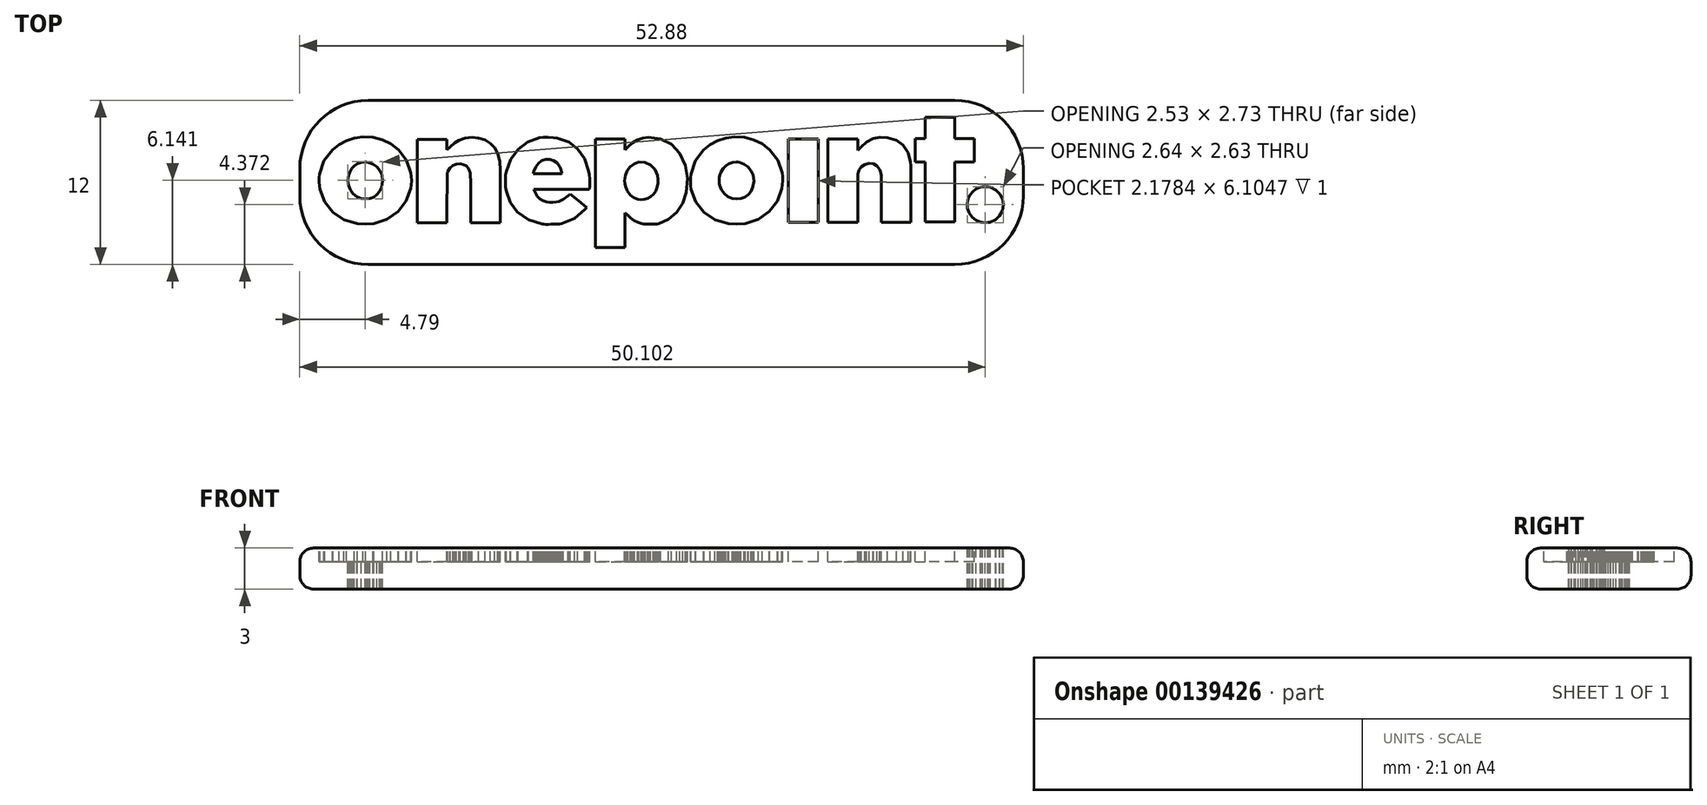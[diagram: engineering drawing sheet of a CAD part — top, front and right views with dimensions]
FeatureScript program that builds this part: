
annotation { "Feature Type Name" : "Feature", "Feature Type Description" : "" }
export const myFeature = defineFeature(function(context is Context, id is Id, definition is map)
    precondition{}
    {
        {
            var Q0;
            Q0=qCreatedBy(makeId("Top.planeOp"),FACE);
            var sketch = newSketch(context, id + "F0", { "sketchPlane" : qUnion([Q0])});
            skLineSegment(sketch, "E0", {"start": v(-22.22, -3.02) * mm, "end": v(-23.2, -2.73) * mm});
            skLineSegment(sketch, "E1", {"start": v(-23.2, -2.73) * mm, "end": v(-24, -2.19) * mm});
            skLineSegment(sketch, "E2", {"start": v(-24, -2.19) * mm, "end": v(-24.6, -1.44) * mm});
            skLineSegment(sketch, "E3", {"start": v(-24.6, -1.44) * mm, "end": v(-24.94, -0.52) * mm});
            skLineSegment(sketch, "E4", {"start": v(-24.94, -0.52) * mm, "end": v(-24.98, -0.27) * mm});
            skLineSegment(sketch, "E5", {"start": v(-24.98, -0.27) * mm, "end": v(-25, 0.03) * mm});
            skLineSegment(sketch, "E6", {"start": v(-25, 0.03) * mm, "end": v(-25, 0.33) * mm});
            skLineSegment(sketch, "E7", {"start": v(-25, 0.33) * mm, "end": v(-24.97, 0.6) * mm});
            skLineSegment(sketch, "E8", {"start": v(-24.97, 0.6) * mm, "end": v(-24.65, 1.57) * mm});
            skLineSegment(sketch, "E9", {"start": v(-24.65, 1.57) * mm, "end": v(-24.03, 2.4) * mm});
            skLineSegment(sketch, "E10", {"start": v(-24.03, 2.4) * mm, "end": v(-23.55, 2.77) * mm});
            skLineSegment(sketch, "E11", {"start": v(-23.55, 2.77) * mm, "end": v(-23.02, 3.06) * mm});
            skLineSegment(sketch, "E12", {"start": v(-23.02, 3.06) * mm, "end": v(-22.43, 3.24) * mm});
            skLineSegment(sketch, "E13", {"start": v(-22.43, 3.24) * mm, "end": v(-21.79, 3.32) * mm});
            skLineSegment(sketch, "E14", {"start": v(-21.79, 3.32) * mm, "end": v(-21.06, 3.29) * mm});
            skLineSegment(sketch, "E15", {"start": v(-21.06, 3.29) * mm, "end": v(-20.38, 3.12) * mm});
            skLineSegment(sketch, "E16", {"start": v(-20.38, 3.12) * mm, "end": v(-19.76, 2.82) * mm});
            skLineSegment(sketch, "E17", {"start": v(-19.76, 2.82) * mm, "end": v(-19.21, 2.4) * mm});
            skLineSegment(sketch, "E18", {"start": v(-19.21, 2.4) * mm, "end": v(-18.61, 1.6) * mm});
            skLineSegment(sketch, "E19", {"start": v(-18.61, 1.6) * mm, "end": v(-18.3, 0.69) * mm});
            skLineSegment(sketch, "E20", {"start": v(-18.3, 0.69) * mm, "end": v(-18.26, 0.43) * mm});
            skLineSegment(sketch, "E21", {"start": v(-18.26, 0.43) * mm, "end": v(-18.26, 0.12) * mm});
            skLineSegment(sketch, "E22", {"start": v(-18.26, 0.12) * mm, "end": v(-18.27, -0.18) * mm});
            skLineSegment(sketch, "E23", {"start": v(-18.27, -0.18) * mm, "end": v(-18.3, -0.44) * mm});
            skLineSegment(sketch, "E24", {"start": v(-18.3, -0.44) * mm, "end": v(-18.64, -1.38) * mm});
            skLineSegment(sketch, "E25", {"start": v(-18.64, -1.38) * mm, "end": v(-19.24, -2.14) * mm});
            skLineSegment(sketch, "E26", {"start": v(-19.24, -2.14) * mm, "end": v(-20.04, -2.7) * mm});
            skLineSegment(sketch, "E27", {"start": v(-20.04, -2.7) * mm, "end": v(-21, -3) * mm});
            skLineSegment(sketch, "E28", {"start": v(-21, -3) * mm, "end": v(-21.62, -3.05) * mm});
            skLineSegment(sketch, "E29", {"start": v(-21.62, -3.05) * mm, "end": v(-22.22, -3.02) * mm});
            skLineSegment(sketch, "E30", {"start": v(-22.22, -3.02) * mm, "end": v(-22.22, -3.02) * mm});
            skLineSegment(sketch, "E31", {"start": v(-21.3, -1.19) * mm, "end": v(-21.02, -1.07) * mm});
            skLineSegment(sketch, "E32", {"start": v(-21.02, -1.07) * mm, "end": v(-20.78, -0.9) * mm});
            skLineSegment(sketch, "E33", {"start": v(-20.78, -0.9) * mm, "end": v(-20.59, -0.66) * mm});
            skLineSegment(sketch, "E34", {"start": v(-20.59, -0.66) * mm, "end": v(-20.44, -0.36) * mm});
            skLineSegment(sketch, "E35", {"start": v(-20.44, -0.36) * mm, "end": v(-20.36, 0.1) * mm});
            skLineSegment(sketch, "E36", {"start": v(-20.36, 0.1) * mm, "end": v(-20.41, 0.53) * mm});
            skLineSegment(sketch, "E37", {"start": v(-20.41, 0.53) * mm, "end": v(-20.57, 0.87) * mm});
            skLineSegment(sketch, "E38", {"start": v(-20.57, 0.87) * mm, "end": v(-20.8, 1.14) * mm});
            skLineSegment(sketch, "E39", {"start": v(-20.8, 1.14) * mm, "end": v(-21.07, 1.34) * mm});
            skLineSegment(sketch, "E40", {"start": v(-21.07, 1.34) * mm, "end": v(-21.4, 1.46) * mm});
            skLineSegment(sketch, "E41", {"start": v(-21.4, 1.46) * mm, "end": v(-21.54, 1.5) * mm});
            skLineSegment(sketch, "E42", {"start": v(-21.54, 1.5) * mm, "end": v(-21.65, 1.5) * mm});
            skLineSegment(sketch, "E43", {"start": v(-21.65, 1.5) * mm, "end": v(-21.92, 1.46) * mm});
            skLineSegment(sketch, "E44", {"start": v(-21.92, 1.46) * mm, "end": v(-22.2, 1.36) * mm});
            skLineSegment(sketch, "E45", {"start": v(-22.2, 1.36) * mm, "end": v(-22.42, 1.21) * mm});
            skLineSegment(sketch, "E46", {"start": v(-22.42, 1.21) * mm, "end": v(-22.61, 1) * mm});
            skLineSegment(sketch, "E47", {"start": v(-22.61, 1) * mm, "end": v(-22.76, 0.77) * mm});
            skLineSegment(sketch, "E48", {"start": v(-22.76, 0.77) * mm, "end": v(-22.85, 0.52) * mm});
            skLineSegment(sketch, "E49", {"start": v(-22.85, 0.52) * mm, "end": v(-22.88, 0.34) * mm});
            skLineSegment(sketch, "E50", {"start": v(-22.88, 0.34) * mm, "end": v(-22.9, 0.14) * mm});
            skLineSegment(sketch, "E51", {"start": v(-22.9, 0.14) * mm, "end": v(-22.88, -0.06) * mm});
            skLineSegment(sketch, "E52", {"start": v(-22.88, -0.06) * mm, "end": v(-22.85, -0.21) * mm});
            skLineSegment(sketch, "E53", {"start": v(-22.85, -0.21) * mm, "end": v(-22.72, -0.55) * mm});
            skLineSegment(sketch, "E54", {"start": v(-22.72, -0.55) * mm, "end": v(-22.52, -0.84) * mm});
            skLineSegment(sketch, "E55", {"start": v(-22.52, -0.84) * mm, "end": v(-22.25, -1.06) * mm});
            skLineSegment(sketch, "E56", {"start": v(-22.25, -1.06) * mm, "end": v(-21.93, -1.19) * mm});
            skLineSegment(sketch, "E57", {"start": v(-21.93, -1.19) * mm, "end": v(-21.62, -1.22) * mm});
            skLineSegment(sketch, "E58", {"start": v(-21.62, -1.22) * mm, "end": v(-21.3, -1.19) * mm});
            skLineSegment(sketch, "E59", {"start": v(-21.3, -1.19) * mm, "end": v(-21.3, -1.19) * mm});
            skLineSegment(sketch, "E60", {"start": v(-17.82, 0.1) * mm, "end": v(-17.82, 3.15) * mm});
            skLineSegment(sketch, "E61", {"start": v(-17.82, 3.15) * mm, "end": v(-15.66, 3.15) * mm});
            skLineSegment(sketch, "E62", {"start": v(-15.66, 3.15) * mm, "end": v(-15.66, 2.36) * mm});
            skLineSegment(sketch, "E63", {"start": v(-15.66, 2.36) * mm, "end": v(-15.43, 2.6) * mm});
            skLineSegment(sketch, "E64", {"start": v(-15.43, 2.6) * mm, "end": v(-15.1, 2.89) * mm});
            skLineSegment(sketch, "E65", {"start": v(-15.1, 2.89) * mm, "end": v(-14.77, 3.08) * mm});
            skLineSegment(sketch, "E66", {"start": v(-14.77, 3.08) * mm, "end": v(-14.32, 3.24) * mm});
            skLineSegment(sketch, "E67", {"start": v(-14.32, 3.24) * mm, "end": v(-13.83, 3.3) * mm});
            skLineSegment(sketch, "E68", {"start": v(-13.83, 3.3) * mm, "end": v(-13.34, 3.25) * mm});
            skLineSegment(sketch, "E69", {"start": v(-13.34, 3.25) * mm, "end": v(-12.88, 3.1) * mm});
            skLineSegment(sketch, "E70", {"start": v(-12.88, 3.1) * mm, "end": v(-12.5, 2.86) * mm});
            skLineSegment(sketch, "E71", {"start": v(-12.5, 2.86) * mm, "end": v(-12.2, 2.54) * mm});
            skLineSegment(sketch, "E72", {"start": v(-12.2, 2.54) * mm, "end": v(-11.97, 2.13) * mm});
            skLineSegment(sketch, "E73", {"start": v(-11.97, 2.13) * mm, "end": v(-11.82, 1.63) * mm});
            skLineSegment(sketch, "E74", {"start": v(-11.82, 1.63) * mm, "end": v(-11.8, 1.57) * mm});
            skLineSegment(sketch, "E75", {"start": v(-11.8, 1.57) * mm, "end": v(-11.8, 1.47) * mm});
            skLineSegment(sketch, "E76", {"start": v(-11.8, 1.47) * mm, "end": v(-11.78, 1.32) * mm});
            skLineSegment(sketch, "E77", {"start": v(-11.78, 1.32) * mm, "end": v(-11.78, 1.11) * mm});
            skLineSegment(sketch, "E78", {"start": v(-11.78, 1.11) * mm, "end": v(-11.77, 0.82) * mm});
            skLineSegment(sketch, "E79", {"start": v(-11.77, 0.82) * mm, "end": v(-11.77, 0.42) * mm});
            skLineSegment(sketch, "E80", {"start": v(-11.77, 0.42) * mm, "end": v(-11.76, -0.1) * mm});
            skLineSegment(sketch, "E81", {"start": v(-11.76, -0.1) * mm, "end": v(-11.76, -0.75) * mm});
            skLineSegment(sketch, "E82", {"start": v(-11.76, -0.75) * mm, "end": v(-11.76, -2.95) * mm});
            skLineSegment(sketch, "E83", {"start": v(-11.76, -2.95) * mm, "end": v(-13.92, -2.95) * mm});
            skLineSegment(sketch, "E84", {"start": v(-13.92, -2.95) * mm, "end": v(-13.92, -1.18) * mm});
            skLineSegment(sketch, "E85", {"start": v(-13.92, -1.18) * mm, "end": v(-13.93, -0.6) * mm});
            skLineSegment(sketch, "E86", {"start": v(-13.93, -0.6) * mm, "end": v(-13.93, -0.15) * mm});
            skLineSegment(sketch, "E87", {"start": v(-13.93, -0.15) * mm, "end": v(-13.94, 0.17) * mm});
            skLineSegment(sketch, "E88", {"start": v(-13.94, 0.17) * mm, "end": v(-13.94, 0.4) * mm});
            skLineSegment(sketch, "E89", {"start": v(-13.94, 0.4) * mm, "end": v(-13.95, 0.55) * mm});
            skLineSegment(sketch, "E90", {"start": v(-13.95, 0.55) * mm, "end": v(-13.96, 0.64) * mm});
            skLineSegment(sketch, "E91", {"start": v(-13.96, 0.64) * mm, "end": v(-13.97, 0.7) * mm});
            skLineSegment(sketch, "E92", {"start": v(-13.97, 0.7) * mm, "end": v(-13.98, 0.76) * mm});
            skLineSegment(sketch, "E93", {"start": v(-13.98, 0.76) * mm, "end": v(-14.1, 1) * mm});
            skLineSegment(sketch, "E94", {"start": v(-14.1, 1) * mm, "end": v(-14.25, 1.19) * mm});
            skLineSegment(sketch, "E95", {"start": v(-14.25, 1.19) * mm, "end": v(-14.45, 1.3) * mm});
            skLineSegment(sketch, "E96", {"start": v(-14.45, 1.3) * mm, "end": v(-14.7, 1.36) * mm});
            skLineSegment(sketch, "E97", {"start": v(-14.7, 1.36) * mm, "end": v(-14.99, 1.34) * mm});
            skLineSegment(sketch, "E98", {"start": v(-14.99, 1.34) * mm, "end": v(-15.24, 1.24) * mm});
            skLineSegment(sketch, "E99", {"start": v(-15.24, 1.24) * mm, "end": v(-15.45, 1.05) * mm});
            skLineSegment(sketch, "E100", {"start": v(-15.45, 1.05) * mm, "end": v(-15.6, 0.79) * mm});
            skLineSegment(sketch, "E101", {"start": v(-15.6, 0.79) * mm, "end": v(-15.62, 0.74) * mm});
            skLineSegment(sketch, "E102", {"start": v(-15.62, 0.74) * mm, "end": v(-15.63, 0.68) * mm});
            skLineSegment(sketch, "E103", {"start": v(-15.63, 0.68) * mm, "end": v(-15.63, 0.59) * mm});
            skLineSegment(sketch, "E104", {"start": v(-15.63, 0.59) * mm, "end": v(-15.64, 0.44) * mm});
            skLineSegment(sketch, "E105", {"start": v(-15.64, 0.44) * mm, "end": v(-15.65, 0.21) * mm});
            skLineSegment(sketch, "E106", {"start": v(-15.65, 0.21) * mm, "end": v(-15.65, -0.11) * mm});
            skLineSegment(sketch, "E107", {"start": v(-15.65, -0.11) * mm, "end": v(-15.65, -0.56) * mm});
            skLineSegment(sketch, "E108", {"start": v(-15.65, -0.56) * mm, "end": v(-15.66, -1.15) * mm});
            skLineSegment(sketch, "E109", {"start": v(-15.66, -1.15) * mm, "end": v(-15.66, -2.95) * mm});
            skLineSegment(sketch, "E110", {"start": v(-15.66, -2.95) * mm, "end": v(-17.82, -2.95) * mm});
            skLineSegment(sketch, "E111", {"start": v(-17.82, -2.95) * mm, "end": v(-17.82, 0.1) * mm});
            skLineSegment(sketch, "E112", {"start": v(-17.82, 0.1) * mm, "end": v(-17.82, 0.1) * mm});
            skLineSegment(sketch, "E113", {"start": v(-8.68, -3.05) * mm, "end": v(-9.7, -2.75) * mm});
            skLineSegment(sketch, "E114", {"start": v(-9.7, -2.75) * mm, "end": v(-10.51, -2.16) * mm});
            skLineSegment(sketch, "E115", {"start": v(-10.51, -2.16) * mm, "end": v(-11.03, -1.47) * mm});
            skLineSegment(sketch, "E116", {"start": v(-11.03, -1.47) * mm, "end": v(-11.33, -0.63) * mm});
            skLineSegment(sketch, "E117", {"start": v(-11.33, -0.63) * mm, "end": v(-11.36, -0.5) * mm});
            skLineSegment(sketch, "E118", {"start": v(-11.36, -0.5) * mm, "end": v(-11.37, -0.35) * mm});
            skLineSegment(sketch, "E119", {"start": v(-11.37, -0.35) * mm, "end": v(-11.38, -0.17) * mm});
            skLineSegment(sketch, "E120", {"start": v(-11.38, -0.17) * mm, "end": v(-11.39, 0.09) * mm});
            skLineSegment(sketch, "E121", {"start": v(-11.39, 0.09) * mm, "end": v(-11.38, 0.35) * mm});
            skLineSegment(sketch, "E122", {"start": v(-11.38, 0.35) * mm, "end": v(-11.37, 0.53) * mm});
            skLineSegment(sketch, "E123", {"start": v(-11.37, 0.53) * mm, "end": v(-11.36, 0.66) * mm});
            skLineSegment(sketch, "E124", {"start": v(-11.36, 0.66) * mm, "end": v(-11.33, 0.8) * mm});
            skLineSegment(sketch, "E125", {"start": v(-11.33, 0.8) * mm, "end": v(-11.01, 1.7) * mm});
            skLineSegment(sketch, "E126", {"start": v(-11.01, 1.7) * mm, "end": v(-10.47, 2.42) * mm});
            skLineSegment(sketch, "E127", {"start": v(-10.47, 2.42) * mm, "end": v(-9.76, 2.96) * mm});
            skLineSegment(sketch, "E128", {"start": v(-9.76, 2.96) * mm, "end": v(-8.9, 3.25) * mm});
            skLineSegment(sketch, "E129", {"start": v(-8.9, 3.25) * mm, "end": v(-8.62, 3.29) * mm});
            skLineSegment(sketch, "E130", {"start": v(-8.62, 3.29) * mm, "end": v(-8.26, 3.3) * mm});
            skLineSegment(sketch, "E131", {"start": v(-8.26, 3.3) * mm, "end": v(-7.9, 3.28) * mm});
            skLineSegment(sketch, "E132", {"start": v(-7.9, 3.28) * mm, "end": v(-7.6, 3.24) * mm});
            skLineSegment(sketch, "E133", {"start": v(-7.6, 3.24) * mm, "end": v(-6.76, 2.95) * mm});
            skLineSegment(sketch, "E134", {"start": v(-6.76, 2.95) * mm, "end": v(-6.1, 2.44) * mm});
            skLineSegment(sketch, "E135", {"start": v(-6.1, 2.44) * mm, "end": v(-5.61, 1.73) * mm});
            skLineSegment(sketch, "E136", {"start": v(-5.61, 1.73) * mm, "end": v(-5.3, 0.85) * mm});
            skLineSegment(sketch, "E137", {"start": v(-5.3, 0.85) * mm, "end": v(-5.27, 0.57) * mm});
            skLineSegment(sketch, "E138", {"start": v(-5.27, 0.57) * mm, "end": v(-5.24, 0.24) * mm});
            skLineSegment(sketch, "E139", {"start": v(-5.24, 0.24) * mm, "end": v(-5.22, -0.08) * mm});
            skLineSegment(sketch, "E140", {"start": v(-5.22, -0.08) * mm, "end": v(-5.22, -0.32) * mm});
            skLineSegment(sketch, "E141", {"start": v(-5.22, -0.32) * mm, "end": v(-5.25, -0.5) * mm});
            skLineSegment(sketch, "E142", {"start": v(-5.25, -0.5) * mm, "end": v(-9.3, -0.5) * mm});
            skLineSegment(sketch, "E143", {"start": v(-9.3, -0.5) * mm, "end": v(-9.3, -0.56) * mm});
            skLineSegment(sketch, "E144", {"start": v(-9.3, -0.56) * mm, "end": v(-9.27, -0.64) * mm});
            skLineSegment(sketch, "E145", {"start": v(-9.27, -0.64) * mm, "end": v(-9.2, -0.77) * mm});
            skLineSegment(sketch, "E146", {"start": v(-9.2, -0.77) * mm, "end": v(-9.06, -1) * mm});
            skLineSegment(sketch, "E147", {"start": v(-9.06, -1) * mm, "end": v(-8.87, -1.2) * mm});
            skLineSegment(sketch, "E148", {"start": v(-8.87, -1.2) * mm, "end": v(-8.64, -1.34) * mm});
            skLineSegment(sketch, "E149", {"start": v(-8.64, -1.34) * mm, "end": v(-8.38, -1.43) * mm});
            skLineSegment(sketch, "E150", {"start": v(-8.38, -1.43) * mm, "end": v(-8.16, -1.46) * mm});
            skLineSegment(sketch, "E151", {"start": v(-8.16, -1.46) * mm, "end": v(-7.92, -1.46) * mm});
            skLineSegment(sketch, "E152", {"start": v(-7.92, -1.46) * mm, "end": v(-7.68, -1.44) * mm});
            skLineSegment(sketch, "E153", {"start": v(-7.68, -1.44) * mm, "end": v(-7.47, -1.4) * mm});
            skLineSegment(sketch, "E154", {"start": v(-7.47, -1.4) * mm, "end": v(-7.15, -1.23) * mm});
            skLineSegment(sketch, "E155", {"start": v(-7.15, -1.23) * mm, "end": v(-6.83, -0.99) * mm});
            skLineSegment(sketch, "E156", {"start": v(-6.83, -0.99) * mm, "end": v(-6.66, -0.85) * mm});
            skLineSegment(sketch, "E157", {"start": v(-6.66, -0.85) * mm, "end": v(-6.05, -1.35) * mm});
            skLineSegment(sketch, "E158", {"start": v(-6.05, -1.35) * mm, "end": v(-5.45, -1.85) * mm});
            skLineSegment(sketch, "E159", {"start": v(-5.45, -1.85) * mm, "end": v(-5.57, -1.98) * mm});
            skLineSegment(sketch, "E160", {"start": v(-5.57, -1.98) * mm, "end": v(-6.33, -2.63) * mm});
            skLineSegment(sketch, "E161", {"start": v(-6.33, -2.63) * mm, "end": v(-7.29, -3) * mm});
            skLineSegment(sketch, "E162", {"start": v(-7.29, -3) * mm, "end": v(-7.43, -3.04) * mm});
            skLineSegment(sketch, "E163", {"start": v(-7.43, -3.04) * mm, "end": v(-7.58, -3.05) * mm});
            skLineSegment(sketch, "E164", {"start": v(-7.58, -3.05) * mm, "end": v(-7.77, -3.06) * mm});
            skLineSegment(sketch, "E165", {"start": v(-7.77, -3.06) * mm, "end": v(-8.05, -3.07) * mm});
            skLineSegment(sketch, "E166", {"start": v(-8.05, -3.07) * mm, "end": v(-8.25, -3.07) * mm});
            skLineSegment(sketch, "E167", {"start": v(-8.25, -3.07) * mm, "end": v(-8.44, -3.07) * mm});
            skLineSegment(sketch, "E168", {"start": v(-8.44, -3.07) * mm, "end": v(-8.59, -3.06) * mm});
            skLineSegment(sketch, "E169", {"start": v(-8.59, -3.06) * mm, "end": v(-8.68, -3.05) * mm});
            skLineSegment(sketch, "E170", {"start": v(-8.68, -3.05) * mm, "end": v(-8.68, -3.05) * mm});
            skLineSegment(sketch, "E171", {"start": v(-7.26, 0.66) * mm, "end": v(-7.27, 0.75) * mm});
            skLineSegment(sketch, "E172", {"start": v(-7.27, 0.75) * mm, "end": v(-7.31, 0.88) * mm});
            skLineSegment(sketch, "E173", {"start": v(-7.31, 0.88) * mm, "end": v(-7.36, 1.02) * mm});
            skLineSegment(sketch, "E174", {"start": v(-7.36, 1.02) * mm, "end": v(-7.42, 1.15) * mm});
            skLineSegment(sketch, "E175", {"start": v(-7.42, 1.15) * mm, "end": v(-7.6, 1.41) * mm});
            skLineSegment(sketch, "E176", {"start": v(-7.6, 1.41) * mm, "end": v(-7.85, 1.6) * mm});
            skLineSegment(sketch, "E177", {"start": v(-7.85, 1.6) * mm, "end": v(-8.14, 1.7) * mm});
            skLineSegment(sketch, "E178", {"start": v(-8.14, 1.7) * mm, "end": v(-8.46, 1.7) * mm});
            skLineSegment(sketch, "E179", {"start": v(-8.46, 1.7) * mm, "end": v(-8.75, 1.59) * mm});
            skLineSegment(sketch, "E180", {"start": v(-8.75, 1.59) * mm, "end": v(-8.99, 1.4) * mm});
            skLineSegment(sketch, "E181", {"start": v(-8.99, 1.4) * mm, "end": v(-9.17, 1.14) * mm});
            skLineSegment(sketch, "E182", {"start": v(-9.17, 1.14) * mm, "end": v(-9.3, 0.8) * mm});
            skLineSegment(sketch, "E183", {"start": v(-9.3, 0.8) * mm, "end": v(-9.35, 0.63) * mm});
            skLineSegment(sketch, "E184", {"start": v(-9.35, 0.63) * mm, "end": v(-8.3, 0.63) * mm});
            skLineSegment(sketch, "E185", {"start": v(-8.3, 0.63) * mm, "end": v(-7.99, 0.63) * mm});
            skLineSegment(sketch, "E186", {"start": v(-7.99, 0.63) * mm, "end": v(-7.74, 0.63) * mm});
            skLineSegment(sketch, "E187", {"start": v(-7.74, 0.63) * mm, "end": v(-7.56, 0.63) * mm});
            skLineSegment(sketch, "E188", {"start": v(-7.56, 0.63) * mm, "end": v(-7.43, 0.63) * mm});
            skLineSegment(sketch, "E189", {"start": v(-7.43, 0.63) * mm, "end": v(-7.34, 0.64) * mm});
            skLineSegment(sketch, "E190", {"start": v(-7.34, 0.64) * mm, "end": v(-7.29, 0.64) * mm});
            skLineSegment(sketch, "E191", {"start": v(-7.29, 0.64) * mm, "end": v(-7.27, 0.65) * mm});
            skLineSegment(sketch, "E192", {"start": v(-7.27, 0.65) * mm, "end": v(-7.26, 0.66) * mm});
            skLineSegment(sketch, "E193", {"start": v(-7.26, 0.66) * mm, "end": v(-7.26, 0.66) * mm});
            skLineSegment(sketch, "E194", {"start": v(-4.8, -0.79) * mm, "end": v(-4.8, 3.17) * mm});
            skLineSegment(sketch, "E195", {"start": v(-4.8, 3.17) * mm, "end": v(-2.64, 3.17) * mm});
            skLineSegment(sketch, "E196", {"start": v(-2.64, 3.17) * mm, "end": v(-2.64, 2.38) * mm});
            skLineSegment(sketch, "E197", {"start": v(-2.64, 2.38) * mm, "end": v(-2.44, 2.6) * mm});
            skLineSegment(sketch, "E198", {"start": v(-2.44, 2.6) * mm, "end": v(-2.1, 2.9) * mm});
            skLineSegment(sketch, "E199", {"start": v(-2.1, 2.9) * mm, "end": v(-1.74, 3.1) * mm});
            skLineSegment(sketch, "E200", {"start": v(-1.74, 3.1) * mm, "end": v(-1.36, 3.24) * mm});
            skLineSegment(sketch, "E201", {"start": v(-1.36, 3.24) * mm, "end": v(-0.92, 3.3) * mm});
            skLineSegment(sketch, "E202", {"start": v(-0.92, 3.3) * mm, "end": v(-0.04, 3.18) * mm});
            skLineSegment(sketch, "E203", {"start": v(-0.04, 3.18) * mm, "end": v(0.74, 2.78) * mm});
            skLineSegment(sketch, "E204", {"start": v(0.74, 2.78) * mm, "end": v(1.35, 2.12) * mm});
            skLineSegment(sketch, "E205", {"start": v(1.35, 2.12) * mm, "end": v(1.76, 1.25) * mm});
            skLineSegment(sketch, "E206", {"start": v(1.76, 1.25) * mm, "end": v(1.9, 0.27) * mm});
            skLineSegment(sketch, "E207", {"start": v(1.9, 0.27) * mm, "end": v(1.83, -0.73) * mm});
            skLineSegment(sketch, "E208", {"start": v(1.83, -0.73) * mm, "end": v(1.56, -1.53) * mm});
            skLineSegment(sketch, "E209", {"start": v(1.56, -1.53) * mm, "end": v(1.12, -2.2) * mm});
            skLineSegment(sketch, "E210", {"start": v(1.12, -2.2) * mm, "end": v(0.54, -2.7) * mm});
            skLineSegment(sketch, "E211", {"start": v(0.54, -2.7) * mm, "end": v(-0.17, -3) * mm});
            skLineSegment(sketch, "E212", {"start": v(-0.17, -3) * mm, "end": v(-0.3, -3.04) * mm});
            skLineSegment(sketch, "E213", {"start": v(-0.3, -3.04) * mm, "end": v(-0.43, -3.06) * mm});
            skLineSegment(sketch, "E214", {"start": v(-0.43, -3.06) * mm, "end": v(-0.58, -3.07) * mm});
            skLineSegment(sketch, "E215", {"start": v(-0.58, -3.07) * mm, "end": v(-0.8, -3.07) * mm});
            skLineSegment(sketch, "E216", {"start": v(-0.8, -3.07) * mm, "end": v(-1.02, -3.07) * mm});
            skLineSegment(sketch, "E217", {"start": v(-1.02, -3.07) * mm, "end": v(-1.17, -3.06) * mm});
            skLineSegment(sketch, "E218", {"start": v(-1.17, -3.06) * mm, "end": v(-1.3, -3.04) * mm});
            skLineSegment(sketch, "E219", {"start": v(-1.3, -3.04) * mm, "end": v(-1.43, -3) * mm});
            skLineSegment(sketch, "E220", {"start": v(-1.43, -3) * mm, "end": v(-1.71, -2.91) * mm});
            skLineSegment(sketch, "E221", {"start": v(-1.71, -2.91) * mm, "end": v(-1.98, -2.78) * mm});
            skLineSegment(sketch, "E222", {"start": v(-1.98, -2.78) * mm, "end": v(-2.23, -2.61) * mm});
            skLineSegment(sketch, "E223", {"start": v(-2.23, -2.61) * mm, "end": v(-2.47, -2.4) * mm});
            skLineSegment(sketch, "E224", {"start": v(-2.47, -2.4) * mm, "end": v(-2.64, -2.24) * mm});
            skLineSegment(sketch, "E225", {"start": v(-2.64, -2.24) * mm, "end": v(-2.64, -4.76) * mm});
            skLineSegment(sketch, "E226", {"start": v(-2.64, -4.76) * mm, "end": v(-4.8, -4.76) * mm});
            skLineSegment(sketch, "E227", {"start": v(-4.8, -4.76) * mm, "end": v(-4.8, -0.79) * mm});
            skLineSegment(sketch, "E228", {"start": v(-4.8, -0.79) * mm, "end": v(-4.8, -0.79) * mm});
            skLineSegment(sketch, "E229", {"start": v(-1.25, -1.25) * mm, "end": v(-1, -1.18) * mm});
            skLineSegment(sketch, "E230", {"start": v(-1, -1.18) * mm, "end": v(-0.77, -1.04) * mm});
            skLineSegment(sketch, "E231", {"start": v(-0.77, -1.04) * mm, "end": v(-0.56, -0.85) * mm});
            skLineSegment(sketch, "E232", {"start": v(-0.56, -0.85) * mm, "end": v(-0.4, -0.63) * mm});
            skLineSegment(sketch, "E233", {"start": v(-0.4, -0.63) * mm, "end": v(-0.3, -0.36) * mm});
            skLineSegment(sketch, "E234", {"start": v(-0.3, -0.36) * mm, "end": v(-0.24, -0.07) * mm});
            skLineSegment(sketch, "E235", {"start": v(-0.24, -0.07) * mm, "end": v(-0.23, 0.23) * mm});
            skLineSegment(sketch, "E236", {"start": v(-0.23, 0.23) * mm, "end": v(-0.28, 0.52) * mm});
            skLineSegment(sketch, "E237", {"start": v(-0.28, 0.52) * mm, "end": v(-0.47, 0.95) * mm});
            skLineSegment(sketch, "E238", {"start": v(-0.47, 0.95) * mm, "end": v(-0.78, 1.27) * mm});
            skLineSegment(sketch, "E239", {"start": v(-0.78, 1.27) * mm, "end": v(-1.18, 1.45) * mm});
            skLineSegment(sketch, "E240", {"start": v(-1.18, 1.45) * mm, "end": v(-1.63, 1.48) * mm});
            skLineSegment(sketch, "E241", {"start": v(-1.63, 1.48) * mm, "end": v(-1.97, 1.37) * mm});
            skLineSegment(sketch, "E242", {"start": v(-1.97, 1.37) * mm, "end": v(-2.26, 1.16) * mm});
            skLineSegment(sketch, "E243", {"start": v(-2.26, 1.16) * mm, "end": v(-2.49, 0.86) * mm});
            skLineSegment(sketch, "E244", {"start": v(-2.49, 0.86) * mm, "end": v(-2.63, 0.5) * mm});
            skLineSegment(sketch, "E245", {"start": v(-2.63, 0.5) * mm, "end": v(-2.66, 0.33) * mm});
            skLineSegment(sketch, "E246", {"start": v(-2.66, 0.33) * mm, "end": v(-2.67, 0.11) * mm});
            skLineSegment(sketch, "E247", {"start": v(-2.67, 0.11) * mm, "end": v(-2.66, -0.1) * mm});
            skLineSegment(sketch, "E248", {"start": v(-2.66, -0.1) * mm, "end": v(-2.63, -0.27) * mm});
            skLineSegment(sketch, "E249", {"start": v(-2.63, -0.27) * mm, "end": v(-2.5, -0.62) * mm});
            skLineSegment(sketch, "E250", {"start": v(-2.5, -0.62) * mm, "end": v(-2.29, -0.9) * mm});
            skLineSegment(sketch, "E251", {"start": v(-2.29, -0.9) * mm, "end": v(-2.02, -1.12) * mm});
            skLineSegment(sketch, "E252", {"start": v(-2.02, -1.12) * mm, "end": v(-1.7, -1.25) * mm});
            skLineSegment(sketch, "E253", {"start": v(-1.7, -1.25) * mm, "end": v(-1.48, -1.27) * mm});
            skLineSegment(sketch, "E254", {"start": v(-1.48, -1.27) * mm, "end": v(-1.25, -1.25) * mm});
            skLineSegment(sketch, "E255", {"start": v(9.3, 0.11) * mm, "end": v(9.3, 3.17) * mm});
            skLineSegment(sketch, "E256", {"start": v(9.3, 3.17) * mm, "end": v(11.47, 3.17) * mm});
            skLineSegment(sketch, "E257", {"start": v(11.47, 3.17) * mm, "end": v(11.47, -2.94) * mm});
            skLineSegment(sketch, "E258", {"start": v(11.47, -2.94) * mm, "end": v(9.3, -2.94) * mm});
            skLineSegment(sketch, "E259", {"start": v(9.3, -2.94) * mm, "end": v(9.3, 0.11) * mm});
            skLineSegment(sketch, "E260", {"start": v(4.9, -3.02) * mm, "end": v(3.94, -2.73) * mm});
            skLineSegment(sketch, "E261", {"start": v(3.94, -2.73) * mm, "end": v(3.13, -2.19) * mm});
            skLineSegment(sketch, "E262", {"start": v(3.13, -2.19) * mm, "end": v(2.54, -1.44) * mm});
            skLineSegment(sketch, "E263", {"start": v(2.54, -1.44) * mm, "end": v(2.19, -0.52) * mm});
            skLineSegment(sketch, "E264", {"start": v(2.19, -0.52) * mm, "end": v(2.14, -0.27) * mm});
            skLineSegment(sketch, "E265", {"start": v(2.14, -0.27) * mm, "end": v(2.13, 0.03) * mm});
            skLineSegment(sketch, "E266", {"start": v(2.13, 0.03) * mm, "end": v(2.13, 0.33) * mm});
            skLineSegment(sketch, "E267", {"start": v(2.13, 0.33) * mm, "end": v(2.16, 0.6) * mm});
            skLineSegment(sketch, "E268", {"start": v(2.16, 0.6) * mm, "end": v(2.48, 1.57) * mm});
            skLineSegment(sketch, "E269", {"start": v(2.48, 1.57) * mm, "end": v(3.1, 2.4) * mm});
            skLineSegment(sketch, "E270", {"start": v(3.1, 2.4) * mm, "end": v(3.58, 2.77) * mm});
            skLineSegment(sketch, "E271", {"start": v(3.58, 2.77) * mm, "end": v(4.11, 3.06) * mm});
            skLineSegment(sketch, "E272", {"start": v(4.11, 3.06) * mm, "end": v(4.7, 3.24) * mm});
            skLineSegment(sketch, "E273", {"start": v(4.7, 3.24) * mm, "end": v(5.34, 3.32) * mm});
            skLineSegment(sketch, "E274", {"start": v(5.34, 3.32) * mm, "end": v(6.07, 3.29) * mm});
            skLineSegment(sketch, "E275", {"start": v(6.07, 3.29) * mm, "end": v(6.75, 3.12) * mm});
            skLineSegment(sketch, "E276", {"start": v(6.75, 3.12) * mm, "end": v(7.37, 2.82) * mm});
            skLineSegment(sketch, "E277", {"start": v(7.37, 2.82) * mm, "end": v(7.92, 2.4) * mm});
            skLineSegment(sketch, "E278", {"start": v(7.92, 2.4) * mm, "end": v(8.52, 1.6) * mm});
            skLineSegment(sketch, "E279", {"start": v(8.52, 1.6) * mm, "end": v(8.84, 0.69) * mm});
            skLineSegment(sketch, "E280", {"start": v(8.84, 0.69) * mm, "end": v(8.86, 0.43) * mm});
            skLineSegment(sketch, "E281", {"start": v(8.86, 0.43) * mm, "end": v(8.87, 0.12) * mm});
            skLineSegment(sketch, "E282", {"start": v(8.87, 0.12) * mm, "end": v(8.85, -0.18) * mm});
            skLineSegment(sketch, "E283", {"start": v(8.85, -0.18) * mm, "end": v(8.82, -0.44) * mm});
            skLineSegment(sketch, "E284", {"start": v(8.82, -0.44) * mm, "end": v(8.48, -1.38) * mm});
            skLineSegment(sketch, "E285", {"start": v(8.48, -1.38) * mm, "end": v(7.9, -2.14) * mm});
            skLineSegment(sketch, "E286", {"start": v(7.9, -2.14) * mm, "end": v(7.1, -2.7) * mm});
            skLineSegment(sketch, "E287", {"start": v(7.1, -2.7) * mm, "end": v(6.13, -3) * mm});
            skLineSegment(sketch, "E288", {"start": v(6.13, -3) * mm, "end": v(5.51, -3.05) * mm});
            skLineSegment(sketch, "E289", {"start": v(5.51, -3.05) * mm, "end": v(4.9, -3.02) * mm});
            skLineSegment(sketch, "E290", {"start": v(5.83, -1.19) * mm, "end": v(6.11, -1.07) * mm});
            skLineSegment(sketch, "E291", {"start": v(6.11, -1.07) * mm, "end": v(6.35, -0.9) * mm});
            skLineSegment(sketch, "E292", {"start": v(6.35, -0.9) * mm, "end": v(6.54, -0.66) * mm});
            skLineSegment(sketch, "E293", {"start": v(6.54, -0.66) * mm, "end": v(6.69, -0.36) * mm});
            skLineSegment(sketch, "E294", {"start": v(6.69, -0.36) * mm, "end": v(6.76, 0.1) * mm});
            skLineSegment(sketch, "E295", {"start": v(6.76, 0.1) * mm, "end": v(6.71, 0.53) * mm});
            skLineSegment(sketch, "E296", {"start": v(6.71, 0.53) * mm, "end": v(6.56, 0.87) * mm});
            skLineSegment(sketch, "E297", {"start": v(6.56, 0.87) * mm, "end": v(6.34, 1.14) * mm});
            skLineSegment(sketch, "E298", {"start": v(6.34, 1.14) * mm, "end": v(6.06, 1.34) * mm});
            skLineSegment(sketch, "E299", {"start": v(6.06, 1.34) * mm, "end": v(5.72, 1.46) * mm});
            skLineSegment(sketch, "E300", {"start": v(5.72, 1.46) * mm, "end": v(5.59, 1.5) * mm});
            skLineSegment(sketch, "E301", {"start": v(5.59, 1.5) * mm, "end": v(5.48, 1.5) * mm});
            skLineSegment(sketch, "E302", {"start": v(5.48, 1.5) * mm, "end": v(5.2, 1.46) * mm});
            skLineSegment(sketch, "E303", {"start": v(5.2, 1.46) * mm, "end": v(4.92, 1.36) * mm});
            skLineSegment(sketch, "E304", {"start": v(4.92, 1.36) * mm, "end": v(4.7, 1.21) * mm});
            skLineSegment(sketch, "E305", {"start": v(4.7, 1.21) * mm, "end": v(4.51, 1) * mm});
            skLineSegment(sketch, "E306", {"start": v(4.51, 1) * mm, "end": v(4.37, 0.77) * mm});
            skLineSegment(sketch, "E307", {"start": v(4.37, 0.77) * mm, "end": v(4.28, 0.52) * mm});
            skLineSegment(sketch, "E308", {"start": v(4.28, 0.52) * mm, "end": v(4.24, 0.34) * mm});
            skLineSegment(sketch, "E309", {"start": v(4.24, 0.34) * mm, "end": v(4.23, 0.14) * mm});
            skLineSegment(sketch, "E310", {"start": v(4.23, 0.14) * mm, "end": v(4.24, -0.06) * mm});
            skLineSegment(sketch, "E311", {"start": v(4.24, -0.06) * mm, "end": v(4.28, -0.21) * mm});
            skLineSegment(sketch, "E312", {"start": v(4.28, -0.21) * mm, "end": v(4.4, -0.55) * mm});
            skLineSegment(sketch, "E313", {"start": v(4.4, -0.55) * mm, "end": v(4.61, -0.84) * mm});
            skLineSegment(sketch, "E314", {"start": v(4.61, -0.84) * mm, "end": v(4.88, -1.06) * mm});
            skLineSegment(sketch, "E315", {"start": v(4.88, -1.06) * mm, "end": v(5.2, -1.19) * mm});
            skLineSegment(sketch, "E316", {"start": v(5.2, -1.19) * mm, "end": v(5.5, -1.22) * mm});
            skLineSegment(sketch, "E317", {"start": v(5.5, -1.22) * mm, "end": v(5.82, -1.19) * mm});
            skLineSegment(sketch, "E318", {"start": v(5.82, -1.19) * mm, "end": v(5.83, -1.19) * mm});
            skLineSegment(sketch, "E319", {"start": v(12.19, 0.11) * mm, "end": v(12.19, 3.17) * mm});
            skLineSegment(sketch, "E320", {"start": v(12.19, 3.17) * mm, "end": v(14.35, 3.17) * mm});
            skLineSegment(sketch, "E321", {"start": v(14.35, 3.17) * mm, "end": v(14.35, 2.35) * mm});
            skLineSegment(sketch, "E322", {"start": v(14.35, 2.35) * mm, "end": v(14.58, 2.58) * mm});
            skLineSegment(sketch, "E323", {"start": v(14.58, 2.58) * mm, "end": v(15.01, 2.95) * mm});
            skLineSegment(sketch, "E324", {"start": v(15.01, 2.95) * mm, "end": v(15.48, 3.2) * mm});
            skLineSegment(sketch, "E325", {"start": v(15.48, 3.2) * mm, "end": v(15.98, 3.3) * mm});
            skLineSegment(sketch, "E326", {"start": v(15.98, 3.3) * mm, "end": v(16.53, 3.28) * mm});
            skLineSegment(sketch, "E327", {"start": v(16.53, 3.28) * mm, "end": v(17.18, 3.09) * mm});
            skLineSegment(sketch, "E328", {"start": v(17.18, 3.09) * mm, "end": v(17.68, 2.71) * mm});
            skLineSegment(sketch, "E329", {"start": v(17.68, 2.71) * mm, "end": v(18.04, 2.17) * mm});
            skLineSegment(sketch, "E330", {"start": v(18.04, 2.17) * mm, "end": v(18.22, 1.48) * mm});
            skLineSegment(sketch, "E331", {"start": v(18.22, 1.48) * mm, "end": v(18.23, 1.25) * mm});
            skLineSegment(sketch, "E332", {"start": v(18.23, 1.25) * mm, "end": v(18.24, 0.75) * mm});
            skLineSegment(sketch, "E333", {"start": v(18.24, 0.75) * mm, "end": v(18.25, 0.05) * mm});
            skLineSegment(sketch, "E334", {"start": v(18.25, 0.05) * mm, "end": v(18.25, -0.82) * mm});
            skLineSegment(sketch, "E335", {"start": v(18.25, -0.82) * mm, "end": v(18.25, -2.94) * mm});
            skLineSegment(sketch, "E336", {"start": v(18.25, -2.94) * mm, "end": v(16.09, -2.94) * mm});
            skLineSegment(sketch, "E337", {"start": v(16.09, -2.94) * mm, "end": v(16.09, -1.2) * mm});
            skLineSegment(sketch, "E338", {"start": v(16.09, -1.2) * mm, "end": v(16.08, -0.58) * mm});
            skLineSegment(sketch, "E339", {"start": v(16.08, -0.58) * mm, "end": v(16.08, -0.1) * mm});
            skLineSegment(sketch, "E340", {"start": v(16.08, -0.1) * mm, "end": v(16.08, 0.25) * mm});
            skLineSegment(sketch, "E341", {"start": v(16.08, 0.25) * mm, "end": v(16.07, 0.5) * mm});
            skLineSegment(sketch, "E342", {"start": v(16.07, 0.5) * mm, "end": v(16.05, 0.67) * mm});
            skLineSegment(sketch, "E343", {"start": v(16.05, 0.67) * mm, "end": v(16.03, 0.8) * mm});
            skLineSegment(sketch, "E344", {"start": v(16.03, 0.8) * mm, "end": v(16, 0.88) * mm});
            skLineSegment(sketch, "E345", {"start": v(16, 0.88) * mm, "end": v(15.96, 0.96) * mm});
            skLineSegment(sketch, "E346", {"start": v(15.96, 0.96) * mm, "end": v(15.76, 1.2) * mm});
            skLineSegment(sketch, "E347", {"start": v(15.76, 1.2) * mm, "end": v(15.5, 1.35) * mm});
            skLineSegment(sketch, "E348", {"start": v(15.5, 1.35) * mm, "end": v(15.18, 1.38) * mm});
            skLineSegment(sketch, "E349", {"start": v(15.18, 1.38) * mm, "end": v(14.87, 1.3) * mm});
            skLineSegment(sketch, "E350", {"start": v(14.87, 1.3) * mm, "end": v(14.63, 1.14) * mm});
            skLineSegment(sketch, "E351", {"start": v(14.63, 1.14) * mm, "end": v(14.47, 0.9) * mm});
            skLineSegment(sketch, "E352", {"start": v(14.47, 0.9) * mm, "end": v(14.43, 0.82) * mm});
            skLineSegment(sketch, "E353", {"start": v(14.43, 0.82) * mm, "end": v(14.4, 0.72) * mm});
            skLineSegment(sketch, "E354", {"start": v(14.4, 0.72) * mm, "end": v(14.38, 0.6) * mm});
            skLineSegment(sketch, "E355", {"start": v(14.38, 0.6) * mm, "end": v(14.36, 0.43) * mm});
            skLineSegment(sketch, "E356", {"start": v(14.36, 0.43) * mm, "end": v(14.36, 0.18) * mm});
            skLineSegment(sketch, "E357", {"start": v(14.36, 0.18) * mm, "end": v(14.35, -0.17) * mm});
            skLineSegment(sketch, "E358", {"start": v(14.35, -0.17) * mm, "end": v(14.35, -0.63) * mm});
            skLineSegment(sketch, "E359", {"start": v(14.35, -0.63) * mm, "end": v(14.35, -1.23) * mm});
            skLineSegment(sketch, "E360", {"start": v(14.35, -1.23) * mm, "end": v(14.35, -2.94) * mm});
            skLineSegment(sketch, "E361", {"start": v(14.35, -2.94) * mm, "end": v(12.19, -2.94) * mm});
            skLineSegment(sketch, "E362", {"start": v(12.19, -2.94) * mm, "end": v(12.19, 0.11) * mm});
            skLineSegment(sketch, "E363", {"start": v(12.19, 0.11) * mm, "end": v(12.19, 0.11) * mm});
            skLineSegment(sketch, "E364", {"start": v(19.3, -0.72) * mm, "end": v(19.3, 1.48) * mm});
            skLineSegment(sketch, "E365", {"start": v(19.3, 1.48) * mm, "end": v(18.56, 1.48) * mm});
            skLineSegment(sketch, "E366", {"start": v(18.56, 1.48) * mm, "end": v(18.56, 3.2) * mm});
            skLineSegment(sketch, "E367", {"start": v(18.56, 3.2) * mm, "end": v(19.3, 3.2) * mm});
            skLineSegment(sketch, "E368", {"start": v(19.3, 3.2) * mm, "end": v(19.3, 4.76) * mm});
            skLineSegment(sketch, "E369", {"start": v(19.3, 4.76) * mm, "end": v(21.46, 4.76) * mm});
            skLineSegment(sketch, "E370", {"start": v(21.46, 4.76) * mm, "end": v(21.46, 3.2) * mm});
            skLineSegment(sketch, "E371", {"start": v(21.46, 3.2) * mm, "end": v(22.86, 3.2) * mm});
            skLineSegment(sketch, "E372", {"start": v(22.86, 3.2) * mm, "end": v(22.86, 1.48) * mm});
            skLineSegment(sketch, "E373", {"start": v(22.86, 1.48) * mm, "end": v(21.46, 1.48) * mm});
            skLineSegment(sketch, "E374", {"start": v(21.46, 1.48) * mm, "end": v(21.46, -2.9) * mm});
            skLineSegment(sketch, "E375", {"start": v(21.46, -2.9) * mm, "end": v(19.3, -2.9) * mm});
            skLineSegment(sketch, "E376", {"start": v(19.3, -2.9) * mm, "end": v(19.3, -0.72) * mm});
            skLineSegment(sketch, "E377", {"start": v(23.34, -2.9) * mm, "end": v(23, -2.76) * mm});
            skLineSegment(sketch, "E378", {"start": v(23, -2.76) * mm, "end": v(22.72, -2.53) * mm});
            skLineSegment(sketch, "E379", {"start": v(22.72, -2.53) * mm, "end": v(22.5, -2.23) * mm});
            skLineSegment(sketch, "E380", {"start": v(22.5, -2.23) * mm, "end": v(22.38, -1.9) * mm});
            skLineSegment(sketch, "E381", {"start": v(22.38, -1.9) * mm, "end": v(22.36, -1.72) * mm});
            skLineSegment(sketch, "E382", {"start": v(22.36, -1.72) * mm, "end": v(22.37, -1.53) * mm});
            skLineSegment(sketch, "E383", {"start": v(22.37, -1.53) * mm, "end": v(22.4, -1.34) * mm});
            skLineSegment(sketch, "E384", {"start": v(22.4, -1.34) * mm, "end": v(22.44, -1.19) * mm});
            skLineSegment(sketch, "E385", {"start": v(22.44, -1.19) * mm, "end": v(22.57, -0.91) * mm});
            skLineSegment(sketch, "E386", {"start": v(22.57, -0.91) * mm, "end": v(22.76, -0.68) * mm});
            skLineSegment(sketch, "E387", {"start": v(22.76, -0.68) * mm, "end": v(23.01, -0.5) * mm});
            skLineSegment(sketch, "E388", {"start": v(23.01, -0.5) * mm, "end": v(23.3, -0.36) * mm});
            skLineSegment(sketch, "E389", {"start": v(23.3, -0.36) * mm, "end": v(23.47, -0.33) * mm});
            skLineSegment(sketch, "E390", {"start": v(23.47, -0.33) * mm, "end": v(23.68, -0.32) * mm});
            skLineSegment(sketch, "E391", {"start": v(23.68, -0.32) * mm, "end": v(23.89, -0.33) * mm});
            skLineSegment(sketch, "E392", {"start": v(23.89, -0.33) * mm, "end": v(24.05, -0.36) * mm});
            skLineSegment(sketch, "E393", {"start": v(24.05, -0.36) * mm, "end": v(24.45, -0.56) * mm});
            skLineSegment(sketch, "E394", {"start": v(24.45, -0.56) * mm, "end": v(24.75, -0.85) * mm});
            skLineSegment(sketch, "E395", {"start": v(24.75, -0.85) * mm, "end": v(24.93, -1.21) * mm});
            skLineSegment(sketch, "E396", {"start": v(24.93, -1.21) * mm, "end": v(25, -1.63) * mm});
            skLineSegment(sketch, "E397", {"start": v(25, -1.63) * mm, "end": v(24.93, -2.06) * mm});
            skLineSegment(sketch, "E398", {"start": v(24.93, -2.06) * mm, "end": v(24.72, -2.44) * mm});
            skLineSegment(sketch, "E399", {"start": v(24.72, -2.44) * mm, "end": v(24.41, -2.73) * mm});
            skLineSegment(sketch, "E400", {"start": v(24.41, -2.73) * mm, "end": v(24.03, -2.9) * mm});
            skLineSegment(sketch, "E401", {"start": v(24.03, -2.9) * mm, "end": v(23.87, -2.93) * mm});
            skLineSegment(sketch, "E402", {"start": v(23.87, -2.93) * mm, "end": v(23.68, -2.94) * mm});
            skLineSegment(sketch, "E403", {"start": v(23.68, -2.94) * mm, "end": v(23.49, -2.93) * mm});
            skLineSegment(sketch, "E404", {"start": v(23.49, -2.93) * mm, "end": v(23.34, -2.9) * mm});
            skLineSegment(sketch, "E405", {"start": v(23.34, -2.9) * mm, "end": v(23.34, -2.9) * mm});
            skLineSegment(sketch, "E406.bottom", {"start": v(-26.42, 6) * mm, "end": v(26.46, 6) * mm});
            skLineSegment(sketch, "E406.top", {"start": v(-26.42, -6) * mm, "end": v(26.46, -6) * mm});
            skLineSegment(sketch, "E406.left", {"start": v(-26.42, 6) * mm, "end": v(-26.42, -6) * mm});
            skLineSegment(sketch, "E406.right", {"start": v(26.46, 6) * mm, "end": v(26.46, -6) * mm});
            skPoint(sketch, "E407.center.orphan", {"position": v(-26.42, 0) * mm});
            skSolve(sketch);
        }
        {
            var Q0;
            {var subQ0=sQuery(id+"F0.wireOp",EDGE,"E28");Q0=makeQuery(id+"F0.imprint","IMPRINT",FACE,{"disambiguationData":[TD([[makeQuery(id+"F0.imprint","IMPRINT",EDGE,{"derivedFrom":subQ0}),1.0]])]});}
            var Q1;
            {var subQ1=sQuery(id+"F0.wireOp",EDGE,"E406.left");var subQ3=sQuery(id+"F0.wireOp",EDGE,"nbQwOtKQ-dwMD-VNoc-CTXo-uGX5Or9HLHrd");var subQ4=makeQuery(id+"F0.imprint","INTERSECT",VERTEX,{"disambiguationData":[OD(0.0)],"derivedFrom":[subQ1,subQ3]});Q1=makeQuery(id+"F0.imprint","IMPRINT",FACE,{"disambiguationData":[TD([[makeQuery(id+"F0.imprint","IMPRINT",EDGE,{"disambiguationData":[TD([[subQ4,-1.0]])],"derivedFrom":subQ3}),-1.0]])]});}
            var Q2;
            Q2=makeQuery(id+"F0.imprint","IMPRINT",FACE,{"disambiguationData":[TD([[makeQuery(id+"F0.imprint","IMPRINT",EDGE,{"derivedFrom":sQuery(id+"F0.wireOp",EDGE,"E319")}),-1.0]])]});
            var Q3;
            Q3=makeQuery(id+"F0.imprint","IMPRINT",FACE,{"disambiguationData":[TD([[makeQuery(id+"F0.imprint","IMPRINT",EDGE,{"derivedFrom":sQuery(id+"F0.wireOp",EDGE,"E229")}),1.0]])]});
            var Q4;
            Q4=makeQuery(id+"F0.imprint","IMPRINT",FACE,{"disambiguationData":[TD([[makeQuery(id+"F0.imprint","IMPRINT",EDGE,{"derivedFrom":sQuery(id+"F0.wireOp",EDGE,"E60")}),-1.0]])]});
            var Q5;
            {var subQ10=sQuery(id+"F0.wireOp",EDGE,"E1");Q5=makeQuery(id+"F0.imprint","IMPRINT",FACE,{"disambiguationData":[TD([[makeQuery(id+"F0.imprint","IMPRINT",EDGE,{"derivedFrom":subQ10}),-1.0]])]});}
            var Q6;
            {var subQ0=sQuery(id+"F0.wireOp",EDGE,"E16");Q6=makeQuery(id+"F0.imprint","IMPRINT",FACE,{"disambiguationData":[TD([[makeQuery(id+"F0.imprint","IMPRINT",EDGE,{"derivedFrom":subQ0}),1.0]])]});}
            var Q7;
            {var subQ8=sQuery(id+"F0.wireOp",EDGE,"E12");Q7=makeQuery(id+"F0.imprint","IMPRINT",FACE,{"disambiguationData":[TD([[makeQuery(id+"F0.imprint","IMPRINT",EDGE,{"derivedFrom":subQ8}),-1.0]])]});}
            var Q8;
            {var subQ10=sQuery(id+"F0.wireOp",EDGE,"E12");Q8=makeQuery(id+"F0.imprint","IMPRINT",FACE,{"disambiguationData":[TD([[makeQuery(id+"F0.imprint","IMPRINT",EDGE,{"derivedFrom":subQ10}),1.0]])]});}
            var Q9;
            Q9=makeQuery(id+"F0.imprint","IMPRINT",FACE,{"disambiguationData":[TD([[makeQuery(id+"F0.imprint","IMPRINT",EDGE,{"derivedFrom":sQuery(id+"F0.wireOp",EDGE,"E364")}),-1.0]])]});
            var Q10;
            {var subQ5=sQuery(id+"F0.wireOp",EDGE,"E16");Q10=makeQuery(id+"F0.imprint","IMPRINT",FACE,{"disambiguationData":[TD([[makeQuery(id+"F0.imprint","IMPRINT",EDGE,{"derivedFrom":subQ5}),-1.0]])]});}
            var Q11;
            Q11=makeQuery(id+"F0.imprint","IMPRINT",FACE,{"disambiguationData":[TD([[makeQuery(id+"F0.imprint","IMPRINT",EDGE,{"derivedFrom":sQuery(id+"F0.wireOp",EDGE,"E113")}),-1.0]])]});
            var Q12;
            Q12=makeQuery(id+"F0.imprint","IMPRINT",FACE,{"disambiguationData":[TD([[makeQuery(id+"F0.imprint","IMPRINT",EDGE,{"derivedFrom":sQuery(id+"F0.wireOp",EDGE,"E194")}),-1.0]])]});
            var Q13;
            Q13=makeQuery(id+"F0.imprint","IMPRINT",FACE,{"disambiguationData":[TD([[makeQuery(id+"F0.imprint","IMPRINT",EDGE,{"derivedFrom":sQuery(id+"F0.wireOp",EDGE,"E290")}),1.0]])]});
            var Q14;
            Q14=makeQuery(id+"F0.imprint","IMPRINT",FACE,{"disambiguationData":[TD([[makeQuery(id+"F0.imprint","IMPRINT",EDGE,{"derivedFrom":sQuery(id+"F0.wireOp",EDGE,"E255")}),-1.0]])]});
            var Q15;
            Q15=makeQuery(id+"F0.imprint","IMPRINT",FACE,{"disambiguationData":[TD([[makeQuery(id+"F0.imprint","IMPRINT",EDGE,{"derivedFrom":sQuery(id+"F0.wireOp",EDGE,"E260")}),-1.0]])]});
            var Q16;
            Q16=makeQuery(id+"F0.imprint","IMPRINT",FACE,{"disambiguationData":[TD([[makeQuery(id+"F0.imprint","IMPRINT",EDGE,{"derivedFrom":sQuery(id+"F0.wireOp",EDGE,"E377")}),-1.0]])]});
            var Q17;
            Q17=makeQuery(id+"F0.imprint","IMPRINT",FACE,{"disambiguationData":[TD([[makeQuery(id+"F0.imprint","IMPRINT",EDGE,{"derivedFrom":sQuery(id+"F0.wireOp",EDGE,"E171")}),1.0]])]});
            extrude(context, id + "F1", {"entities" : qUnion([Q0, Q1, Q2, Q3, Q4, Q5, Q6, Q7, Q8, Q9, Q10, Q11, Q12, Q13, Q14, Q15, Q16, Q17]), "oppositeDirection" : true, "depth" : 3 * mm});
        }
        {
            var Q0;
            {var subQ10=sQuery(id+"F0.wireOp",EDGE,"E1");Q0=makeQuery(id+"F0.imprint","IMPRINT",FACE,{"disambiguationData":[TD([[makeQuery(id+"F0.imprint","IMPRINT",EDGE,{"derivedFrom":subQ10}),-1.0]])]});}
            var Q1;
            {var subQ8=sQuery(id+"F0.wireOp",EDGE,"E12");Q1=makeQuery(id+"F0.imprint","IMPRINT",FACE,{"disambiguationData":[TD([[makeQuery(id+"F0.imprint","IMPRINT",EDGE,{"derivedFrom":subQ8}),-1.0]])]});}
            var Q2;
            Q2=makeQuery(id+"F0.imprint","IMPRINT",FACE,{"disambiguationData":[TD([[makeQuery(id+"F0.imprint","IMPRINT",EDGE,{"derivedFrom":sQuery(id+"F0.wireOp",EDGE,"E60")}),-1.0]])]});
            var Q3;
            Q3=makeQuery(id+"F0.imprint","IMPRINT",FACE,{"disambiguationData":[TD([[makeQuery(id+"F0.imprint","IMPRINT",EDGE,{"derivedFrom":sQuery(id+"F0.wireOp",EDGE,"E113")}),-1.0]])]});
            var Q4;
            Q4=makeQuery(id+"F0.imprint","IMPRINT",FACE,{"disambiguationData":[TD([[makeQuery(id+"F0.imprint","IMPRINT",EDGE,{"derivedFrom":sQuery(id+"F0.wireOp",EDGE,"E255")}),-1.0]])]});
            var Q5;
            Q5=makeQuery(id+"F0.imprint","IMPRINT",FACE,{"disambiguationData":[TD([[makeQuery(id+"F0.imprint","IMPRINT",EDGE,{"derivedFrom":sQuery(id+"F0.wireOp",EDGE,"E319")}),-1.0]])]});
            var Q6;
            Q6=makeQuery(id+"F0.imprint","IMPRINT",FACE,{"disambiguationData":[TD([[makeQuery(id+"F0.imprint","IMPRINT",EDGE,{"derivedFrom":sQuery(id+"F0.wireOp",EDGE,"E364")}),-1.0]])]});
            var Q7;
            Q7=makeQuery(id+"F0.imprint","IMPRINT",FACE,{"disambiguationData":[TD([[makeQuery(id+"F0.imprint","IMPRINT",EDGE,{"derivedFrom":sQuery(id+"F0.wireOp",EDGE,"E194")}),-1.0]])]});
            var Q8;
            Q8=makeQuery(id+"F0.imprint","IMPRINT",FACE,{"disambiguationData":[TD([[makeQuery(id+"F0.imprint","IMPRINT",EDGE,{"derivedFrom":sQuery(id+"F0.wireOp",EDGE,"E260")}),-1.0]])]});
            var Q9;
            Q9=makeQuery(id+"F0.imprint","IMPRINT",FACE,{"disambiguationData":[TD([[makeQuery(id+"F0.imprint","IMPRINT",EDGE,{"derivedFrom":sQuery(id+"F0.wireOp",EDGE,"E377")}),-1.0]])]});
            var Q10;
            {var subQ5=sQuery(id+"F0.wireOp",EDGE,"E16");Q10=makeQuery(id+"F0.imprint","IMPRINT",FACE,{"disambiguationData":[TD([[makeQuery(id+"F0.imprint","IMPRINT",EDGE,{"derivedFrom":subQ5}),-1.0]])]});}
            extrude(context, id + "F2", {"entities" : qUnion([Q0, Q1, Q2, Q3, Q4, Q5, Q6, Q7, Q8, Q9, Q10]), "operationType" : NewBodyOperationType.REMOVE, "oppositeDirection" : true, "depth" : 1 * mm});
        }
        {
            var Q0;
            Q0=makeQuery(id+"F1.opExtrude","SWEPT_EDGE",EDGE,{"disambiguationData":[OSD([sQuery(id+"F0.wireOp",EDGE,"E406.top"),sQuery(id+"F0.wireOp",EDGE,"E406.right")])]});
            var Q1;
            Q1=makeQuery(id+"F1.opExtrude","SWEPT_EDGE",EDGE,{"disambiguationData":[OSD([sQuery(id+"F0.wireOp",EDGE,"E406.bottom"),sQuery(id+"F0.wireOp",EDGE,"E406.right")])]});
            var Q2;
            Q2=makeQuery(id+"F1.opExtrude","SWEPT_EDGE",EDGE,{"disambiguationData":[OSD([sQuery(id+"F0.wireOp",EDGE,"E406.bottom"),sQuery(id+"F0.wireOp",EDGE,"E406.left")])]});
            var Q3;
            Q3=makeQuery(id+"F1.opExtrude","SWEPT_EDGE",EDGE,{"disambiguationData":[OSD([sQuery(id+"F0.wireOp",EDGE,"E406.top"),sQuery(id+"F0.wireOp",EDGE,"E406.left")])]});
            fillet(context, id + "F3", {"entities" : qUnion([Q0, Q1, Q2, Q3]), "radius" : 5 * mm, "tangentPropagation" : true, "allowEdgeOverflow" : false});
        }
        {
            var Q0;
            Q0=makeQuery(id+"F0.imprint","IMPRINT",FACE,{"disambiguationData":[TD([[makeQuery(id+"F0.imprint","IMPRINT",EDGE,{"derivedFrom":sQuery(id+"F0.wireOp",EDGE,"E377")}),-1.0]])]});
            extrude(context, id + "F4", {"entities" : qUnion([Q0]), "operationType" : NewBodyOperationType.REMOVE, "oppositeDirection" : true, "depth" : 3 * mm});
        }
        {
            var Q0;
            Q0=makeQuery(id+"F1.opExtrude","CAP_EDGE",EDGE,{"disambiguationData":[OSD([sQuery(id+"F0.wireOp",EDGE,"E406.bottom")])],"isStart":true});
            var Q1;
            Q1=makeQuery(id+"F1.opExtrude","CAP_EDGE",EDGE,{"disambiguationData":[OSD([sQuery(id+"F0.wireOp",EDGE,"E407")])],"isStart":true});
            var Q2;
            Q2=makeQuery(id+"F1.opExtrude","CAP_EDGE",EDGE,{"disambiguationData":[OSD([sQuery(id+"F0.wireOp",EDGE,"E406.top")])],"isStart":true});
            var Q3;
            {var subQ0=sQuery(id+"F0.wireOp",EDGE,"E407");var subQ1=sQuery(id+"F0.wireOp",EDGE,"E0");var subQ2=sQuery(id+"F0.wireOp",EDGE,"E406.bottom");var subQ3=sQuery(id+"F0.wireOp",EDGE,"nbQwOtKQ-dwMD-VNoc-CTXo-uGX5Or9HLHrd");var subQ4=sQuery(id+"F0.wireOp",EDGE,"E11");var subQ5=sQuery(id+"F0.wireOp",EDGE,"E406.right");var subQ6=sQuery(id+"F0.wireOp",EDGE,"E406.top");Q3=makeQuery(id+"F3.opFillet","BLEND_EDGE",EDGE,{"blendedFrom":[makeQuery(id+"F1.opExtrude","SWEPT_EDGE",EDGE,{"disambiguationData":[OSD([subQ6,subQ5])]}),makeQuery(id+"F2.boolean.opBoolean","SPLIT",FACE,{"disambiguationData":[TD([makeQuery(id+"F1.opExtrude","SWEPT_FACE",FACE,{"disambiguationData":[OSD([subQ2])]})])],"derivedFrom":makeQuery(id+"F1.opExtrude","CAP_FACE",FACE,{"disambiguationData":[OSD([subQ1,sQuery(id+"F0.wireOp",EDGE,"E1"),sQuery(id+"F0.wireOp",EDGE,"E2"),sQuery(id+"F0.wireOp",EDGE,"E3"),sQuery(id+"F0.wireOp",EDGE,"E4"),sQuery(id+"F0.wireOp",EDGE,"E5"),sQuery(id+"F0.wireOp",EDGE,"E6"),sQuery(id+"F0.wireOp",EDGE,"E7"),sQuery(id+"F0.wireOp",EDGE,"E8"),sQuery(id+"F0.wireOp",EDGE,"E9"),sQuery(id+"F0.wireOp",EDGE,"E10"),subQ4,sQuery(id+"F0.wireOp",EDGE,"E31"),sQuery(id+"F0.wireOp",EDGE,"E32"),sQuery(id+"F0.wireOp",EDGE,"E33"),sQuery(id+"F0.wireOp",EDGE,"E34"),sQuery(id+"F0.wireOp",EDGE,"E35"),sQuery(id+"F0.wireOp",EDGE,"E36"),sQuery(id+"F0.wireOp",EDGE,"E37"),sQuery(id+"F0.wireOp",EDGE,"E38"),sQuery(id+"F0.wireOp",EDGE,"E39"),sQuery(id+"F0.wireOp",EDGE,"E40"),sQuery(id+"F0.wireOp",EDGE,"E41"),sQuery(id+"F0.wireOp",EDGE,"E42"),sQuery(id+"F0.wireOp",EDGE,"E43"),sQuery(id+"F0.wireOp",EDGE,"E44"),sQuery(id+"F0.wireOp",EDGE,"E45"),sQuery(id+"F0.wireOp",EDGE,"E46"),sQuery(id+"F0.wireOp",EDGE,"E47"),sQuery(id+"F0.wireOp",EDGE,"E48"),sQuery(id+"F0.wireOp",EDGE,"E49"),sQuery(id+"F0.wireOp",EDGE,"E50"),sQuery(id+"F0.wireOp",EDGE,"E51"),sQuery(id+"F0.wireOp",EDGE,"E52"),sQuery(id+"F0.wireOp",EDGE,"E53"),sQuery(id+"F0.wireOp",EDGE,"E54"),sQuery(id+"F0.wireOp",EDGE,"E55"),sQuery(id+"F0.wireOp",EDGE,"E56"),sQuery(id+"F0.wireOp",EDGE,"E57"),sQuery(id+"F0.wireOp",EDGE,"E58"),sQuery(id+"F0.wireOp",EDGE,"E59"),subQ2,subQ6,subQ5,subQ0,subQ3])],"isStart":true})})],"blendedInto":[makeQuery(id+"F2.boolean.opBoolean","SPLIT",FACE,{"disambiguationData":[TD([makeQuery(id+"F1.opExtrude","SWEPT_FACE",FACE,{"disambiguationData":[OSD([subQ2])]})])],"derivedFrom":makeQuery(id+"F1.opExtrude","CAP_FACE",FACE,{"disambiguationData":[OSD([subQ1,sQuery(id+"F0.wireOp",EDGE,"E1"),sQuery(id+"F0.wireOp",EDGE,"E2"),sQuery(id+"F0.wireOp",EDGE,"E3"),sQuery(id+"F0.wireOp",EDGE,"E4"),sQuery(id+"F0.wireOp",EDGE,"E5"),sQuery(id+"F0.wireOp",EDGE,"E6"),sQuery(id+"F0.wireOp",EDGE,"E7"),sQuery(id+"F0.wireOp",EDGE,"E8"),sQuery(id+"F0.wireOp",EDGE,"E9"),sQuery(id+"F0.wireOp",EDGE,"E10"),subQ4,sQuery(id+"F0.wireOp",EDGE,"E31"),sQuery(id+"F0.wireOp",EDGE,"E32"),sQuery(id+"F0.wireOp",EDGE,"E33"),sQuery(id+"F0.wireOp",EDGE,"E34"),sQuery(id+"F0.wireOp",EDGE,"E35"),sQuery(id+"F0.wireOp",EDGE,"E36"),sQuery(id+"F0.wireOp",EDGE,"E37"),sQuery(id+"F0.wireOp",EDGE,"E38"),sQuery(id+"F0.wireOp",EDGE,"E39"),sQuery(id+"F0.wireOp",EDGE,"E40"),sQuery(id+"F0.wireOp",EDGE,"E41"),sQuery(id+"F0.wireOp",EDGE,"E42"),sQuery(id+"F0.wireOp",EDGE,"E43"),sQuery(id+"F0.wireOp",EDGE,"E44"),sQuery(id+"F0.wireOp",EDGE,"E45"),sQuery(id+"F0.wireOp",EDGE,"E46"),sQuery(id+"F0.wireOp",EDGE,"E47"),sQuery(id+"F0.wireOp",EDGE,"E48"),sQuery(id+"F0.wireOp",EDGE,"E49"),sQuery(id+"F0.wireOp",EDGE,"E50"),sQuery(id+"F0.wireOp",EDGE,"E51"),sQuery(id+"F0.wireOp",EDGE,"E52"),sQuery(id+"F0.wireOp",EDGE,"E53"),sQuery(id+"F0.wireOp",EDGE,"E54"),sQuery(id+"F0.wireOp",EDGE,"E55"),sQuery(id+"F0.wireOp",EDGE,"E56"),sQuery(id+"F0.wireOp",EDGE,"E57"),sQuery(id+"F0.wireOp",EDGE,"E58"),sQuery(id+"F0.wireOp",EDGE,"E59"),subQ2,subQ6,subQ5,subQ0,subQ3])],"isStart":true})})]});}
            var Q4;
            Q4=makeQuery(id+"F1.opExtrude","CAP_EDGE",EDGE,{"disambiguationData":[OSD([sQuery(id+"F0.wireOp",EDGE,"E406.right")])],"isStart":true});
            var Q5;
            {var subQ0=sQuery(id+"F0.wireOp",EDGE,"E407");var subQ1=sQuery(id+"F0.wireOp",EDGE,"E0");var subQ2=sQuery(id+"F0.wireOp",EDGE,"E406.bottom");var subQ3=sQuery(id+"F0.wireOp",EDGE,"nbQwOtKQ-dwMD-VNoc-CTXo-uGX5Or9HLHrd");var subQ4=sQuery(id+"F0.wireOp",EDGE,"E11");var subQ5=sQuery(id+"F0.wireOp",EDGE,"E406.right");var subQ6=sQuery(id+"F0.wireOp",EDGE,"E406.top");Q5=makeQuery(id+"F3.opFillet","BLEND_EDGE",EDGE,{"blendedFrom":[makeQuery(id+"F1.opExtrude","SWEPT_EDGE",EDGE,{"disambiguationData":[OSD([subQ2,subQ5])]}),makeQuery(id+"F2.boolean.opBoolean","SPLIT",FACE,{"disambiguationData":[TD([makeQuery(id+"F1.opExtrude","SWEPT_FACE",FACE,{"disambiguationData":[OSD([subQ2])]})])],"derivedFrom":makeQuery(id+"F1.opExtrude","CAP_FACE",FACE,{"disambiguationData":[OSD([subQ1,sQuery(id+"F0.wireOp",EDGE,"E1"),sQuery(id+"F0.wireOp",EDGE,"E2"),sQuery(id+"F0.wireOp",EDGE,"E3"),sQuery(id+"F0.wireOp",EDGE,"E4"),sQuery(id+"F0.wireOp",EDGE,"E5"),sQuery(id+"F0.wireOp",EDGE,"E6"),sQuery(id+"F0.wireOp",EDGE,"E7"),sQuery(id+"F0.wireOp",EDGE,"E8"),sQuery(id+"F0.wireOp",EDGE,"E9"),sQuery(id+"F0.wireOp",EDGE,"E10"),subQ4,sQuery(id+"F0.wireOp",EDGE,"E31"),sQuery(id+"F0.wireOp",EDGE,"E32"),sQuery(id+"F0.wireOp",EDGE,"E33"),sQuery(id+"F0.wireOp",EDGE,"E34"),sQuery(id+"F0.wireOp",EDGE,"E35"),sQuery(id+"F0.wireOp",EDGE,"E36"),sQuery(id+"F0.wireOp",EDGE,"E37"),sQuery(id+"F0.wireOp",EDGE,"E38"),sQuery(id+"F0.wireOp",EDGE,"E39"),sQuery(id+"F0.wireOp",EDGE,"E40"),sQuery(id+"F0.wireOp",EDGE,"E41"),sQuery(id+"F0.wireOp",EDGE,"E42"),sQuery(id+"F0.wireOp",EDGE,"E43"),sQuery(id+"F0.wireOp",EDGE,"E44"),sQuery(id+"F0.wireOp",EDGE,"E45"),sQuery(id+"F0.wireOp",EDGE,"E46"),sQuery(id+"F0.wireOp",EDGE,"E47"),sQuery(id+"F0.wireOp",EDGE,"E48"),sQuery(id+"F0.wireOp",EDGE,"E49"),sQuery(id+"F0.wireOp",EDGE,"E50"),sQuery(id+"F0.wireOp",EDGE,"E51"),sQuery(id+"F0.wireOp",EDGE,"E52"),sQuery(id+"F0.wireOp",EDGE,"E53"),sQuery(id+"F0.wireOp",EDGE,"E54"),sQuery(id+"F0.wireOp",EDGE,"E55"),sQuery(id+"F0.wireOp",EDGE,"E56"),sQuery(id+"F0.wireOp",EDGE,"E57"),sQuery(id+"F0.wireOp",EDGE,"E58"),sQuery(id+"F0.wireOp",EDGE,"E59"),subQ2,subQ6,subQ5,subQ0,subQ3])],"isStart":true})})],"blendedInto":[makeQuery(id+"F2.boolean.opBoolean","SPLIT",FACE,{"disambiguationData":[TD([makeQuery(id+"F1.opExtrude","SWEPT_FACE",FACE,{"disambiguationData":[OSD([subQ2])]})])],"derivedFrom":makeQuery(id+"F1.opExtrude","CAP_FACE",FACE,{"disambiguationData":[OSD([subQ1,sQuery(id+"F0.wireOp",EDGE,"E1"),sQuery(id+"F0.wireOp",EDGE,"E2"),sQuery(id+"F0.wireOp",EDGE,"E3"),sQuery(id+"F0.wireOp",EDGE,"E4"),sQuery(id+"F0.wireOp",EDGE,"E5"),sQuery(id+"F0.wireOp",EDGE,"E6"),sQuery(id+"F0.wireOp",EDGE,"E7"),sQuery(id+"F0.wireOp",EDGE,"E8"),sQuery(id+"F0.wireOp",EDGE,"E9"),sQuery(id+"F0.wireOp",EDGE,"E10"),subQ4,sQuery(id+"F0.wireOp",EDGE,"E31"),sQuery(id+"F0.wireOp",EDGE,"E32"),sQuery(id+"F0.wireOp",EDGE,"E33"),sQuery(id+"F0.wireOp",EDGE,"E34"),sQuery(id+"F0.wireOp",EDGE,"E35"),sQuery(id+"F0.wireOp",EDGE,"E36"),sQuery(id+"F0.wireOp",EDGE,"E37"),sQuery(id+"F0.wireOp",EDGE,"E38"),sQuery(id+"F0.wireOp",EDGE,"E39"),sQuery(id+"F0.wireOp",EDGE,"E40"),sQuery(id+"F0.wireOp",EDGE,"E41"),sQuery(id+"F0.wireOp",EDGE,"E42"),sQuery(id+"F0.wireOp",EDGE,"E43"),sQuery(id+"F0.wireOp",EDGE,"E44"),sQuery(id+"F0.wireOp",EDGE,"E45"),sQuery(id+"F0.wireOp",EDGE,"E46"),sQuery(id+"F0.wireOp",EDGE,"E47"),sQuery(id+"F0.wireOp",EDGE,"E48"),sQuery(id+"F0.wireOp",EDGE,"E49"),sQuery(id+"F0.wireOp",EDGE,"E50"),sQuery(id+"F0.wireOp",EDGE,"E51"),sQuery(id+"F0.wireOp",EDGE,"E52"),sQuery(id+"F0.wireOp",EDGE,"E53"),sQuery(id+"F0.wireOp",EDGE,"E54"),sQuery(id+"F0.wireOp",EDGE,"E55"),sQuery(id+"F0.wireOp",EDGE,"E56"),sQuery(id+"F0.wireOp",EDGE,"E57"),sQuery(id+"F0.wireOp",EDGE,"E58"),sQuery(id+"F0.wireOp",EDGE,"E59"),subQ2,subQ6,subQ5,subQ0,subQ3])],"isStart":true})})]});}
            var Q6;
            {var subQ0=sQuery(id+"F0.wireOp",EDGE,"E406.left");var subQ1=sQuery(id+"F0.wireOp",EDGE,"E406.bottom");var subQ2=sQuery(id+"F0.wireOp",EDGE,"E406.right");var subQ3=sQuery(id+"F0.wireOp",EDGE,"E406.top");Q6=makeQuery(id+"F3.opFillet","BLEND_EDGE",EDGE,{"blendedFrom":[makeQuery(id+"F1.opExtrude","SWEPT_EDGE",EDGE,{"disambiguationData":[OSD([subQ1,subQ0])]}),makeQuery(id+"F2.boolean.opBoolean","SPLIT",FACE,{"disambiguationData":[TD([makeQuery(id+"F1.opExtrude","SWEPT_FACE",FACE,{"disambiguationData":[OSD([subQ1])]})])],"derivedFrom":makeQuery(id+"F1.opExtrude","CAP_FACE",FACE,{"disambiguationData":[OSD([sQuery(id+"F0.wireOp",EDGE,"E31"),sQuery(id+"F0.wireOp",EDGE,"E32"),sQuery(id+"F0.wireOp",EDGE,"E33"),sQuery(id+"F0.wireOp",EDGE,"E34"),sQuery(id+"F0.wireOp",EDGE,"E35"),sQuery(id+"F0.wireOp",EDGE,"E36"),sQuery(id+"F0.wireOp",EDGE,"E37"),sQuery(id+"F0.wireOp",EDGE,"E38"),sQuery(id+"F0.wireOp",EDGE,"E39"),sQuery(id+"F0.wireOp",EDGE,"E40"),sQuery(id+"F0.wireOp",EDGE,"E41"),sQuery(id+"F0.wireOp",EDGE,"E42"),sQuery(id+"F0.wireOp",EDGE,"E43"),sQuery(id+"F0.wireOp",EDGE,"E44"),sQuery(id+"F0.wireOp",EDGE,"E45"),sQuery(id+"F0.wireOp",EDGE,"E46"),sQuery(id+"F0.wireOp",EDGE,"E47"),sQuery(id+"F0.wireOp",EDGE,"E48"),sQuery(id+"F0.wireOp",EDGE,"E49"),sQuery(id+"F0.wireOp",EDGE,"E50"),sQuery(id+"F0.wireOp",EDGE,"E51"),sQuery(id+"F0.wireOp",EDGE,"E52"),sQuery(id+"F0.wireOp",EDGE,"E53"),sQuery(id+"F0.wireOp",EDGE,"E54"),sQuery(id+"F0.wireOp",EDGE,"E55"),sQuery(id+"F0.wireOp",EDGE,"E56"),sQuery(id+"F0.wireOp",EDGE,"E57"),sQuery(id+"F0.wireOp",EDGE,"E58"),sQuery(id+"F0.wireOp",EDGE,"E59"),subQ1,subQ3,subQ0,subQ2])],"isStart":true})})],"blendedInto":[makeQuery(id+"F2.boolean.opBoolean","SPLIT",FACE,{"disambiguationData":[TD([makeQuery(id+"F1.opExtrude","SWEPT_FACE",FACE,{"disambiguationData":[OSD([subQ1])]})])],"derivedFrom":makeQuery(id+"F1.opExtrude","CAP_FACE",FACE,{"disambiguationData":[OSD([sQuery(id+"F0.wireOp",EDGE,"E31"),sQuery(id+"F0.wireOp",EDGE,"E32"),sQuery(id+"F0.wireOp",EDGE,"E33"),sQuery(id+"F0.wireOp",EDGE,"E34"),sQuery(id+"F0.wireOp",EDGE,"E35"),sQuery(id+"F0.wireOp",EDGE,"E36"),sQuery(id+"F0.wireOp",EDGE,"E37"),sQuery(id+"F0.wireOp",EDGE,"E38"),sQuery(id+"F0.wireOp",EDGE,"E39"),sQuery(id+"F0.wireOp",EDGE,"E40"),sQuery(id+"F0.wireOp",EDGE,"E41"),sQuery(id+"F0.wireOp",EDGE,"E42"),sQuery(id+"F0.wireOp",EDGE,"E43"),sQuery(id+"F0.wireOp",EDGE,"E44"),sQuery(id+"F0.wireOp",EDGE,"E45"),sQuery(id+"F0.wireOp",EDGE,"E46"),sQuery(id+"F0.wireOp",EDGE,"E47"),sQuery(id+"F0.wireOp",EDGE,"E48"),sQuery(id+"F0.wireOp",EDGE,"E49"),sQuery(id+"F0.wireOp",EDGE,"E50"),sQuery(id+"F0.wireOp",EDGE,"E51"),sQuery(id+"F0.wireOp",EDGE,"E52"),sQuery(id+"F0.wireOp",EDGE,"E53"),sQuery(id+"F0.wireOp",EDGE,"E54"),sQuery(id+"F0.wireOp",EDGE,"E55"),sQuery(id+"F0.wireOp",EDGE,"E56"),sQuery(id+"F0.wireOp",EDGE,"E57"),sQuery(id+"F0.wireOp",EDGE,"E58"),sQuery(id+"F0.wireOp",EDGE,"E59"),subQ1,subQ3,subQ0,subQ2])],"isStart":true})})]});}
            var Q7;
            Q7=makeQuery(id+"F1.opExtrude","CAP_EDGE",EDGE,{"disambiguationData":[OSD([sQuery(id+"F0.wireOp",EDGE,"E406.left")])],"isStart":true});
            var Q8;
            {var subQ0=sQuery(id+"F0.wireOp",EDGE,"E406.left");var subQ1=sQuery(id+"F0.wireOp",EDGE,"E406.bottom");var subQ2=sQuery(id+"F0.wireOp",EDGE,"E406.right");var subQ3=sQuery(id+"F0.wireOp",EDGE,"E406.top");Q8=makeQuery(id+"F3.opFillet","BLEND_EDGE",EDGE,{"blendedFrom":[makeQuery(id+"F1.opExtrude","SWEPT_EDGE",EDGE,{"disambiguationData":[OSD([subQ3,subQ0])]}),makeQuery(id+"F2.boolean.opBoolean","SPLIT",FACE,{"disambiguationData":[TD([makeQuery(id+"F1.opExtrude","SWEPT_FACE",FACE,{"disambiguationData":[OSD([subQ1])]})])],"derivedFrom":makeQuery(id+"F1.opExtrude","CAP_FACE",FACE,{"disambiguationData":[OSD([sQuery(id+"F0.wireOp",EDGE,"E31"),sQuery(id+"F0.wireOp",EDGE,"E32"),sQuery(id+"F0.wireOp",EDGE,"E33"),sQuery(id+"F0.wireOp",EDGE,"E34"),sQuery(id+"F0.wireOp",EDGE,"E35"),sQuery(id+"F0.wireOp",EDGE,"E36"),sQuery(id+"F0.wireOp",EDGE,"E37"),sQuery(id+"F0.wireOp",EDGE,"E38"),sQuery(id+"F0.wireOp",EDGE,"E39"),sQuery(id+"F0.wireOp",EDGE,"E40"),sQuery(id+"F0.wireOp",EDGE,"E41"),sQuery(id+"F0.wireOp",EDGE,"E42"),sQuery(id+"F0.wireOp",EDGE,"E43"),sQuery(id+"F0.wireOp",EDGE,"E44"),sQuery(id+"F0.wireOp",EDGE,"E45"),sQuery(id+"F0.wireOp",EDGE,"E46"),sQuery(id+"F0.wireOp",EDGE,"E47"),sQuery(id+"F0.wireOp",EDGE,"E48"),sQuery(id+"F0.wireOp",EDGE,"E49"),sQuery(id+"F0.wireOp",EDGE,"E50"),sQuery(id+"F0.wireOp",EDGE,"E51"),sQuery(id+"F0.wireOp",EDGE,"E52"),sQuery(id+"F0.wireOp",EDGE,"E53"),sQuery(id+"F0.wireOp",EDGE,"E54"),sQuery(id+"F0.wireOp",EDGE,"E55"),sQuery(id+"F0.wireOp",EDGE,"E56"),sQuery(id+"F0.wireOp",EDGE,"E57"),sQuery(id+"F0.wireOp",EDGE,"E58"),sQuery(id+"F0.wireOp",EDGE,"E59"),subQ1,subQ3,subQ0,subQ2])],"isStart":true})})],"blendedInto":[makeQuery(id+"F2.boolean.opBoolean","SPLIT",FACE,{"disambiguationData":[TD([makeQuery(id+"F1.opExtrude","SWEPT_FACE",FACE,{"disambiguationData":[OSD([subQ1])]})])],"derivedFrom":makeQuery(id+"F1.opExtrude","CAP_FACE",FACE,{"disambiguationData":[OSD([sQuery(id+"F0.wireOp",EDGE,"E31"),sQuery(id+"F0.wireOp",EDGE,"E32"),sQuery(id+"F0.wireOp",EDGE,"E33"),sQuery(id+"F0.wireOp",EDGE,"E34"),sQuery(id+"F0.wireOp",EDGE,"E35"),sQuery(id+"F0.wireOp",EDGE,"E36"),sQuery(id+"F0.wireOp",EDGE,"E37"),sQuery(id+"F0.wireOp",EDGE,"E38"),sQuery(id+"F0.wireOp",EDGE,"E39"),sQuery(id+"F0.wireOp",EDGE,"E40"),sQuery(id+"F0.wireOp",EDGE,"E41"),sQuery(id+"F0.wireOp",EDGE,"E42"),sQuery(id+"F0.wireOp",EDGE,"E43"),sQuery(id+"F0.wireOp",EDGE,"E44"),sQuery(id+"F0.wireOp",EDGE,"E45"),sQuery(id+"F0.wireOp",EDGE,"E46"),sQuery(id+"F0.wireOp",EDGE,"E47"),sQuery(id+"F0.wireOp",EDGE,"E48"),sQuery(id+"F0.wireOp",EDGE,"E49"),sQuery(id+"F0.wireOp",EDGE,"E50"),sQuery(id+"F0.wireOp",EDGE,"E51"),sQuery(id+"F0.wireOp",EDGE,"E52"),sQuery(id+"F0.wireOp",EDGE,"E53"),sQuery(id+"F0.wireOp",EDGE,"E54"),sQuery(id+"F0.wireOp",EDGE,"E55"),sQuery(id+"F0.wireOp",EDGE,"E56"),sQuery(id+"F0.wireOp",EDGE,"E57"),sQuery(id+"F0.wireOp",EDGE,"E58"),sQuery(id+"F0.wireOp",EDGE,"E59"),subQ1,subQ3,subQ0,subQ2])],"isStart":true})})]});}
            fillet(context, id + "F5", {"entities" : qUnion([Q0, Q1, Q2, Q3, Q4, Q5, Q6, Q7, Q8]), "radius" : 1 * mm, "allowEdgeOverflow" : false});
        }
        {
            var Q0;
            Q0=makeQuery(id+"F1.opExtrude","CAP_EDGE",EDGE,{"disambiguationData":[OSD([sQuery(id+"F0.wireOp",EDGE,"E406.top")])],"isStart":false});
            var Q1;
            {var subQ0=sQuery(id+"F0.wireOp",EDGE,"E406.right");var subQ1=sQuery(id+"F0.wireOp",EDGE,"E406.top");Q1=makeQuery(id+"F3.opFillet","BLEND_EDGE",EDGE,{"blendedFrom":[makeQuery(id+"F1.opExtrude","SWEPT_EDGE",EDGE,{"disambiguationData":[OSD([subQ1,subQ0])]}),makeQuery(id+"F1.opExtrude","CAP_FACE",FACE,{"disambiguationData":[OSD([sQuery(id+"F0.wireOp",EDGE,"E0"),sQuery(id+"F0.wireOp",EDGE,"E1"),sQuery(id+"F0.wireOp",EDGE,"E2"),sQuery(id+"F0.wireOp",EDGE,"E3"),sQuery(id+"F0.wireOp",EDGE,"E4"),sQuery(id+"F0.wireOp",EDGE,"E5"),sQuery(id+"F0.wireOp",EDGE,"E6"),sQuery(id+"F0.wireOp",EDGE,"E7"),sQuery(id+"F0.wireOp",EDGE,"E8"),sQuery(id+"F0.wireOp",EDGE,"E9"),sQuery(id+"F0.wireOp",EDGE,"E10"),sQuery(id+"F0.wireOp",EDGE,"E11"),sQuery(id+"F0.wireOp",EDGE,"E31"),sQuery(id+"F0.wireOp",EDGE,"E32"),sQuery(id+"F0.wireOp",EDGE,"E33"),sQuery(id+"F0.wireOp",EDGE,"E34"),sQuery(id+"F0.wireOp",EDGE,"E35"),sQuery(id+"F0.wireOp",EDGE,"E36"),sQuery(id+"F0.wireOp",EDGE,"E37"),sQuery(id+"F0.wireOp",EDGE,"E38"),sQuery(id+"F0.wireOp",EDGE,"E39"),sQuery(id+"F0.wireOp",EDGE,"E40"),sQuery(id+"F0.wireOp",EDGE,"E41"),sQuery(id+"F0.wireOp",EDGE,"E42"),sQuery(id+"F0.wireOp",EDGE,"E43"),sQuery(id+"F0.wireOp",EDGE,"E44"),sQuery(id+"F0.wireOp",EDGE,"E45"),sQuery(id+"F0.wireOp",EDGE,"E46"),sQuery(id+"F0.wireOp",EDGE,"E47"),sQuery(id+"F0.wireOp",EDGE,"E48"),sQuery(id+"F0.wireOp",EDGE,"E49"),sQuery(id+"F0.wireOp",EDGE,"E50"),sQuery(id+"F0.wireOp",EDGE,"E51"),sQuery(id+"F0.wireOp",EDGE,"E52"),sQuery(id+"F0.wireOp",EDGE,"E53"),sQuery(id+"F0.wireOp",EDGE,"E54"),sQuery(id+"F0.wireOp",EDGE,"E55"),sQuery(id+"F0.wireOp",EDGE,"E56"),sQuery(id+"F0.wireOp",EDGE,"E57"),sQuery(id+"F0.wireOp",EDGE,"E58"),sQuery(id+"F0.wireOp",EDGE,"E59"),sQuery(id+"F0.wireOp",EDGE,"E406.bottom"),subQ1,subQ0,sQuery(id+"F0.wireOp",EDGE,"E407"),sQuery(id+"F0.wireOp",EDGE,"nbQwOtKQ-dwMD-VNoc-CTXo-uGX5Or9HLHrd")])],"isStart":false})],"blendedInto":[makeQuery(id+"F1.opExtrude","CAP_FACE",FACE,{"disambiguationData":[OSD([sQuery(id+"F0.wireOp",EDGE,"E0"),sQuery(id+"F0.wireOp",EDGE,"E1"),sQuery(id+"F0.wireOp",EDGE,"E2"),sQuery(id+"F0.wireOp",EDGE,"E3"),sQuery(id+"F0.wireOp",EDGE,"E4"),sQuery(id+"F0.wireOp",EDGE,"E5"),sQuery(id+"F0.wireOp",EDGE,"E6"),sQuery(id+"F0.wireOp",EDGE,"E7"),sQuery(id+"F0.wireOp",EDGE,"E8"),sQuery(id+"F0.wireOp",EDGE,"E9"),sQuery(id+"F0.wireOp",EDGE,"E10"),sQuery(id+"F0.wireOp",EDGE,"E11"),sQuery(id+"F0.wireOp",EDGE,"E31"),sQuery(id+"F0.wireOp",EDGE,"E32"),sQuery(id+"F0.wireOp",EDGE,"E33"),sQuery(id+"F0.wireOp",EDGE,"E34"),sQuery(id+"F0.wireOp",EDGE,"E35"),sQuery(id+"F0.wireOp",EDGE,"E36"),sQuery(id+"F0.wireOp",EDGE,"E37"),sQuery(id+"F0.wireOp",EDGE,"E38"),sQuery(id+"F0.wireOp",EDGE,"E39"),sQuery(id+"F0.wireOp",EDGE,"E40"),sQuery(id+"F0.wireOp",EDGE,"E41"),sQuery(id+"F0.wireOp",EDGE,"E42"),sQuery(id+"F0.wireOp",EDGE,"E43"),sQuery(id+"F0.wireOp",EDGE,"E44"),sQuery(id+"F0.wireOp",EDGE,"E45"),sQuery(id+"F0.wireOp",EDGE,"E46"),sQuery(id+"F0.wireOp",EDGE,"E47"),sQuery(id+"F0.wireOp",EDGE,"E48"),sQuery(id+"F0.wireOp",EDGE,"E49"),sQuery(id+"F0.wireOp",EDGE,"E50"),sQuery(id+"F0.wireOp",EDGE,"E51"),sQuery(id+"F0.wireOp",EDGE,"E52"),sQuery(id+"F0.wireOp",EDGE,"E53"),sQuery(id+"F0.wireOp",EDGE,"E54"),sQuery(id+"F0.wireOp",EDGE,"E55"),sQuery(id+"F0.wireOp",EDGE,"E56"),sQuery(id+"F0.wireOp",EDGE,"E57"),sQuery(id+"F0.wireOp",EDGE,"E58"),sQuery(id+"F0.wireOp",EDGE,"E59"),sQuery(id+"F0.wireOp",EDGE,"E406.bottom"),subQ1,subQ0,sQuery(id+"F0.wireOp",EDGE,"E407"),sQuery(id+"F0.wireOp",EDGE,"nbQwOtKQ-dwMD-VNoc-CTXo-uGX5Or9HLHrd")])],"isStart":false})]});}
            var Q2;
            {var subQ0=sQuery(id+"F0.wireOp",EDGE,"E406.right");var subQ1=sQuery(id+"F0.wireOp",EDGE,"E406.bottom");Q2=makeQuery(id+"F3.opFillet","BLEND_EDGE",EDGE,{"blendedFrom":[makeQuery(id+"F1.opExtrude","SWEPT_EDGE",EDGE,{"disambiguationData":[OSD([subQ1,subQ0])]}),makeQuery(id+"F1.opExtrude","CAP_FACE",FACE,{"disambiguationData":[OSD([sQuery(id+"F0.wireOp",EDGE,"E0"),sQuery(id+"F0.wireOp",EDGE,"E1"),sQuery(id+"F0.wireOp",EDGE,"E2"),sQuery(id+"F0.wireOp",EDGE,"E3"),sQuery(id+"F0.wireOp",EDGE,"E4"),sQuery(id+"F0.wireOp",EDGE,"E5"),sQuery(id+"F0.wireOp",EDGE,"E6"),sQuery(id+"F0.wireOp",EDGE,"E7"),sQuery(id+"F0.wireOp",EDGE,"E8"),sQuery(id+"F0.wireOp",EDGE,"E9"),sQuery(id+"F0.wireOp",EDGE,"E10"),sQuery(id+"F0.wireOp",EDGE,"E11"),sQuery(id+"F0.wireOp",EDGE,"E31"),sQuery(id+"F0.wireOp",EDGE,"E32"),sQuery(id+"F0.wireOp",EDGE,"E33"),sQuery(id+"F0.wireOp",EDGE,"E34"),sQuery(id+"F0.wireOp",EDGE,"E35"),sQuery(id+"F0.wireOp",EDGE,"E36"),sQuery(id+"F0.wireOp",EDGE,"E37"),sQuery(id+"F0.wireOp",EDGE,"E38"),sQuery(id+"F0.wireOp",EDGE,"E39"),sQuery(id+"F0.wireOp",EDGE,"E40"),sQuery(id+"F0.wireOp",EDGE,"E41"),sQuery(id+"F0.wireOp",EDGE,"E42"),sQuery(id+"F0.wireOp",EDGE,"E43"),sQuery(id+"F0.wireOp",EDGE,"E44"),sQuery(id+"F0.wireOp",EDGE,"E45"),sQuery(id+"F0.wireOp",EDGE,"E46"),sQuery(id+"F0.wireOp",EDGE,"E47"),sQuery(id+"F0.wireOp",EDGE,"E48"),sQuery(id+"F0.wireOp",EDGE,"E49"),sQuery(id+"F0.wireOp",EDGE,"E50"),sQuery(id+"F0.wireOp",EDGE,"E51"),sQuery(id+"F0.wireOp",EDGE,"E52"),sQuery(id+"F0.wireOp",EDGE,"E53"),sQuery(id+"F0.wireOp",EDGE,"E54"),sQuery(id+"F0.wireOp",EDGE,"E55"),sQuery(id+"F0.wireOp",EDGE,"E56"),sQuery(id+"F0.wireOp",EDGE,"E57"),sQuery(id+"F0.wireOp",EDGE,"E58"),sQuery(id+"F0.wireOp",EDGE,"E59"),subQ1,sQuery(id+"F0.wireOp",EDGE,"E406.top"),subQ0,sQuery(id+"F0.wireOp",EDGE,"E407"),sQuery(id+"F0.wireOp",EDGE,"nbQwOtKQ-dwMD-VNoc-CTXo-uGX5Or9HLHrd")])],"isStart":false})],"blendedInto":[makeQuery(id+"F1.opExtrude","CAP_FACE",FACE,{"disambiguationData":[OSD([sQuery(id+"F0.wireOp",EDGE,"E0"),sQuery(id+"F0.wireOp",EDGE,"E1"),sQuery(id+"F0.wireOp",EDGE,"E2"),sQuery(id+"F0.wireOp",EDGE,"E3"),sQuery(id+"F0.wireOp",EDGE,"E4"),sQuery(id+"F0.wireOp",EDGE,"E5"),sQuery(id+"F0.wireOp",EDGE,"E6"),sQuery(id+"F0.wireOp",EDGE,"E7"),sQuery(id+"F0.wireOp",EDGE,"E8"),sQuery(id+"F0.wireOp",EDGE,"E9"),sQuery(id+"F0.wireOp",EDGE,"E10"),sQuery(id+"F0.wireOp",EDGE,"E11"),sQuery(id+"F0.wireOp",EDGE,"E31"),sQuery(id+"F0.wireOp",EDGE,"E32"),sQuery(id+"F0.wireOp",EDGE,"E33"),sQuery(id+"F0.wireOp",EDGE,"E34"),sQuery(id+"F0.wireOp",EDGE,"E35"),sQuery(id+"F0.wireOp",EDGE,"E36"),sQuery(id+"F0.wireOp",EDGE,"E37"),sQuery(id+"F0.wireOp",EDGE,"E38"),sQuery(id+"F0.wireOp",EDGE,"E39"),sQuery(id+"F0.wireOp",EDGE,"E40"),sQuery(id+"F0.wireOp",EDGE,"E41"),sQuery(id+"F0.wireOp",EDGE,"E42"),sQuery(id+"F0.wireOp",EDGE,"E43"),sQuery(id+"F0.wireOp",EDGE,"E44"),sQuery(id+"F0.wireOp",EDGE,"E45"),sQuery(id+"F0.wireOp",EDGE,"E46"),sQuery(id+"F0.wireOp",EDGE,"E47"),sQuery(id+"F0.wireOp",EDGE,"E48"),sQuery(id+"F0.wireOp",EDGE,"E49"),sQuery(id+"F0.wireOp",EDGE,"E50"),sQuery(id+"F0.wireOp",EDGE,"E51"),sQuery(id+"F0.wireOp",EDGE,"E52"),sQuery(id+"F0.wireOp",EDGE,"E53"),sQuery(id+"F0.wireOp",EDGE,"E54"),sQuery(id+"F0.wireOp",EDGE,"E55"),sQuery(id+"F0.wireOp",EDGE,"E56"),sQuery(id+"F0.wireOp",EDGE,"E57"),sQuery(id+"F0.wireOp",EDGE,"E58"),sQuery(id+"F0.wireOp",EDGE,"E59"),subQ1,sQuery(id+"F0.wireOp",EDGE,"E406.top"),subQ0,sQuery(id+"F0.wireOp",EDGE,"E407"),sQuery(id+"F0.wireOp",EDGE,"nbQwOtKQ-dwMD-VNoc-CTXo-uGX5Or9HLHrd")])],"isStart":false})]});}
            var Q3;
            Q3=makeQuery(id+"F1.opExtrude","CAP_EDGE",EDGE,{"disambiguationData":[OSD([sQuery(id+"F0.wireOp",EDGE,"E406.right")])],"isStart":false});
            var Q4;
            Q4=makeQuery(id+"F1.opExtrude","CAP_EDGE",EDGE,{"disambiguationData":[OSD([sQuery(id+"F0.wireOp",EDGE,"E406.bottom")])],"isStart":false});
            var Q5;
            Q5=makeQuery(id+"F1.opExtrude","CAP_EDGE",EDGE,{"disambiguationData":[OSD([sQuery(id+"F0.wireOp",EDGE,"E407")])],"isStart":false});
            fillet(context, id + "F6", {"entities" : qUnion([Q0, Q1, Q2, Q3, Q4, Q5]), "radius" : 1 * mm, "tangentPropagation" : true, "allowEdgeOverflow" : false});
        }
    });
